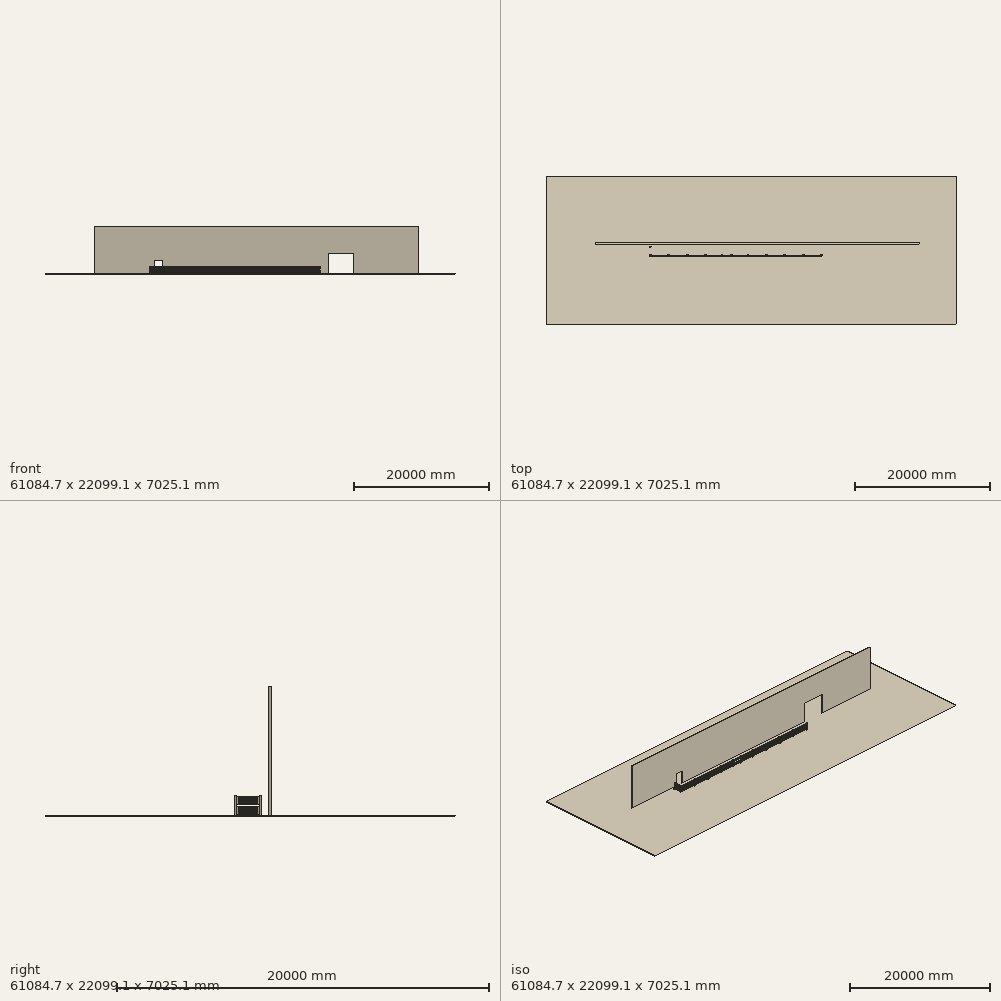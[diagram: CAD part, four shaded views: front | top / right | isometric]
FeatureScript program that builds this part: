
annotation { "Feature Type Name" : "Feature", "Feature Type Description" : "" }
export const myFeature = defineFeature(function(context is Context, id is Id, definition is map)
    precondition{}
    {
        {
            var Q0;
            Q0=qCreatedBy(makeId("Front.planeOp"),FACE);
            var sketch = newSketch(context, id + "F0", { "sketchPlane" : qUnion([Q0])});
            skLineSegment(sketch, "E0.bottom", {"start": v(-8708.65, 6974.33) * mm, "end": v(39551.35, 6974.33) * mm});
            skLineSegment(sketch, "E0.top", {"start": v(-8708.65, 0) * mm, "end": v(181.35, 0) * mm});
            skLineSegment(sketch, "E0.left", {"start": v(-8708.65, 6974.33) * mm, "end": v(-8708.65, 0) * mm});
            skLineSegment(sketch, "E0.right", {"start": v(39551.35, 6974.33) * mm, "end": v(39551.35, 0) * mm});
            skLineSegment(sketch, "E1.bottom", {"start": v(181.35, 1981.2) * mm, "end": v(1400.55, 1981.2) * mm});
            skLineSegment(sketch, "E1.left", {"start": v(181.35, 1981.2) * mm, "end": v(181.35, 0) * mm});
            skLineSegment(sketch, "E1.right", {"start": v(1400.55, 1981.2) * mm, "end": v(1400.55, 0) * mm});
            skLineSegment(sketch, "E2.trimOffspring", {"start": v(1400.55, 0) * mm, "end": v(26165.55, 0) * mm});
            skLineSegment(sketch, "E3.bottom", {"start": v(26165.55, 3048) * mm, "end": v(29823.15, 3048) * mm});
            skLineSegment(sketch, "E3.left", {"start": v(26165.55, 3048) * mm, "end": v(26165.55, 0) * mm});
            skLineSegment(sketch, "E3.right", {"start": v(29823.15, 3048) * mm, "end": v(29823.15, 0) * mm});
            skLineSegment(sketch, "E4.trimOffspring", {"start": v(29823.15, 0) * mm, "end": v(39551.35, 0) * mm});
            skSolve(sketch);
        }
        {
            var Q0;
            Q0 = qSketchRegion(id + "F0", true);
            extrude(context, id + "F1", {"entities" : qUnion([Q0]), "oppositeDirection" : true, "depth" : 152.4 * mm, "offsetDistance" : 25.4 * mm});
        }
        {
            var Q0;
            Q0=qCreatedBy(makeId("Top.planeOp"),FACE);
            var sketch = newSketch(context, id + "F2", { "sketchPlane" : qUnion([Q0])});
            skLineSegment(sketch, "E5.bottom", {"start": v(-16039.74, 10082.5) * mm, "end": v(45045, 10082.5) * mm});
            skLineSegment(sketch, "E5.top", {"start": v(-16039.74, -12016.58) * mm, "end": v(45045, -12016.58) * mm});
            skLineSegment(sketch, "E5.left", {"start": v(-16039.74, 10082.5) * mm, "end": v(-16039.74, -12016.58) * mm});
            skLineSegment(sketch, "E5.right", {"start": v(45045, 10082.5) * mm, "end": v(45045, -12016.58) * mm});
            skSolve(sketch);
        }
        {
            var Q0;
            Q0 = qSketchRegion(id + "F2", true);
            extrude(context, id + "F3", {"entities" : qUnion([Q0]), "oppositeDirection" : true, "depth" : 50.8 * mm, "offsetDistance" : 25.4 * mm});
        }
        {
            var Q0;
            Q0=makeQuery(id+"F3.opExtrude","CAP_FACE",FACE,{"disambiguationData":[OSD([sQuery(id+"F2.wireOp",EDGE,"E5.bottom"),sQuery(id+"F2.wireOp",EDGE,"E5.top"),sQuery(id+"F2.wireOp",EDGE,"E5.left"),sQuery(id+"F2.wireOp",EDGE,"E5.right")])],"isStart":true});
            var sketch = newSketch(context, id + "F4", { "sketchPlane" : qUnion([Q0])});
            skLineSegment(sketch, "E6.bottom", {"start": v(-682.25, -1625.6) * mm, "end": v(-428.25, -1625.6) * mm});
            skLineSegment(sketch, "E6.top", {"start": v(-682.25, -1879.6) * mm, "end": v(-428.25, -1879.6) * mm});
            skLineSegment(sketch, "E6.left", {"start": v(-682.25, -1625.6) * mm, "end": v(-682.25, -1879.6) * mm});
            skLineSegment(sketch, "E6.right", {"start": v(-428.25, -1625.6) * mm, "end": v(-428.25, -1879.6) * mm});
            skLineSegment(sketch, "E7.bottom", {"start": v(-682.25, -304.8) * mm, "end": v(-428.25, -304.8) * mm});
            skLineSegment(sketch, "E7.top", {"start": v(-682.25, -558.8) * mm, "end": v(-428.25, -558.8) * mm});
            skLineSegment(sketch, "E7.left", {"start": v(-682.25, -304.8) * mm, "end": v(-682.25, -558.8) * mm});
            skLineSegment(sketch, "E7.right", {"start": v(-428.25, -304.8) * mm, "end": v(-428.25, -558.8) * mm});
            skLineSegment(sketch, "E8.bottom", {"start": v(2060.95, -1625.6) * mm, "end": v(2314.95, -1625.6) * mm});
            skLineSegment(sketch, "E8.top", {"start": v(2060.95, -1879.6) * mm, "end": v(2314.95, -1879.6) * mm});
            skLineSegment(sketch, "E8.left", {"start": v(2060.95, -1625.6) * mm, "end": v(2060.95, -1879.6) * mm});
            skLineSegment(sketch, "E8.right", {"start": v(2314.95, -1625.6) * mm, "end": v(2314.95, -1879.6) * mm});
            skLineSegment(sketch, "E9.bottom", {"start": v(4804.15, -1625.6) * mm, "end": v(5058.15, -1625.6) * mm});
            skLineSegment(sketch, "E9.top", {"start": v(4804.15, -1879.6) * mm, "end": v(5058.15, -1879.6) * mm});
            skLineSegment(sketch, "E9.left", {"start": v(4804.15, -1625.6) * mm, "end": v(4804.15, -1879.6) * mm});
            skLineSegment(sketch, "E9.right", {"start": v(5058.15, -1625.6) * mm, "end": v(5058.15, -1879.6) * mm});
            skLineSegment(sketch, "E10.bottom", {"start": v(7547.35, -1625.6) * mm, "end": v(7801.35, -1625.6) * mm});
            skLineSegment(sketch, "E10.top", {"start": v(7547.35, -1879.6) * mm, "end": v(7801.35, -1879.6) * mm});
            skLineSegment(sketch, "E10.left", {"start": v(7547.35, -1625.6) * mm, "end": v(7547.35, -1879.6) * mm});
            skLineSegment(sketch, "E10.right", {"start": v(7801.35, -1625.6) * mm, "end": v(7801.35, -1879.6) * mm});
            skLineSegment(sketch, "E11.bottom", {"start": v(9985.75, -1625.6) * mm, "end": v(10239.75, -1625.6) * mm});
            skLineSegment(sketch, "E11.top", {"start": v(9985.75, -1879.6) * mm, "end": v(10239.75, -1879.6) * mm});
            skLineSegment(sketch, "E11.left", {"start": v(9985.75, -1625.6) * mm, "end": v(9985.75, -1879.6) * mm});
            skLineSegment(sketch, "E11.right", {"start": v(10239.75, -1625.6) * mm, "end": v(10239.75, -1879.6) * mm});
            skLineSegment(sketch, "E12.bottom", {"start": v(11408.15, -1625.6) * mm, "end": v(11662.15, -1625.6) * mm});
            skLineSegment(sketch, "E12.top", {"start": v(11408.15, -1879.6) * mm, "end": v(11662.15, -1879.6) * mm});
            skLineSegment(sketch, "E12.left", {"start": v(11408.15, -1625.6) * mm, "end": v(11408.15, -1879.6) * mm});
            skLineSegment(sketch, "E12.right", {"start": v(11662.15, -1625.6) * mm, "end": v(11662.15, -1879.6) * mm});
            skSolve(sketch);
        }
        {
            var Q0;
            Q0 = qSketchRegion(id + "F4", true);
            extrude(context, id + "F5", {"entities" : qUnion([Q0]), "depth" : 15.88 * mm, "offsetDistance" : 25.4 * mm});
        }
        {
            var Q0;
            Q0=makeQuery(id+"F5.opExtrude","CAP_FACE",FACE,{"disambiguationData":[OSD([sQuery(id+"F4.wireOp",EDGE,"E7.bottom"),sQuery(id+"F4.wireOp",EDGE,"E7.top"),sQuery(id+"F4.wireOp",EDGE,"E7.left"),sQuery(id+"F4.wireOp",EDGE,"E7.right")])],"isStart":false});
            var sketch = newSketch(context, id + "F6", { "sketchPlane" : qUnion([Q0])});
            skLineSegment(sketch, "E13.bottom", {"start": v(-606.05, -381) * mm, "end": v(-504.45, -381) * mm});
            skLineSegment(sketch, "E13.top", {"start": v(-606.05, -482.6) * mm, "end": v(-504.45, -482.6) * mm});
            skLineSegment(sketch, "E13.left", {"start": v(-606.05, -381) * mm, "end": v(-606.05, -482.6) * mm});
            skLineSegment(sketch, "E13.right", {"start": v(-504.45, -381) * mm, "end": v(-504.45, -482.6) * mm});
            skLineSegment(sketch, "E14.bottom", {"start": v(-606.05, -1701.8) * mm, "end": v(-504.45, -1701.8) * mm});
            skLineSegment(sketch, "E14.top", {"start": v(-606.05, -1803.4) * mm, "end": v(-504.45, -1803.4) * mm});
            skLineSegment(sketch, "E14.left", {"start": v(-606.05, -1701.8) * mm, "end": v(-606.05, -1803.4) * mm});
            skLineSegment(sketch, "E14.right", {"start": v(-504.45, -1701.8) * mm, "end": v(-504.45, -1803.4) * mm});
            skLineSegment(sketch, "E15.bottom", {"start": v(2137.15, -1701.8) * mm, "end": v(2238.75, -1701.8) * mm});
            skLineSegment(sketch, "E15.top", {"start": v(2137.15, -1803.4) * mm, "end": v(2238.75, -1803.4) * mm});
            skLineSegment(sketch, "E15.left", {"start": v(2137.15, -1701.8) * mm, "end": v(2137.15, -1803.4) * mm});
            skLineSegment(sketch, "E15.right", {"start": v(2238.75, -1701.8) * mm, "end": v(2238.75, -1803.4) * mm});
            skLineSegment(sketch, "E16.bottom", {"start": v(4880.35, -1701.8) * mm, "end": v(4981.95, -1701.8) * mm});
            skLineSegment(sketch, "E16.top", {"start": v(4880.35, -1803.4) * mm, "end": v(4981.95, -1803.4) * mm});
            skLineSegment(sketch, "E16.left", {"start": v(4880.35, -1701.8) * mm, "end": v(4880.35, -1803.4) * mm});
            skLineSegment(sketch, "E16.right", {"start": v(4981.95, -1701.8) * mm, "end": v(4981.95, -1803.4) * mm});
            skLineSegment(sketch, "E17.bottom", {"start": v(7623.55, -1701.8) * mm, "end": v(7725.15, -1701.8) * mm});
            skLineSegment(sketch, "E17.top", {"start": v(7623.55, -1803.4) * mm, "end": v(7725.15, -1803.4) * mm});
            skLineSegment(sketch, "E17.left", {"start": v(7623.55, -1701.8) * mm, "end": v(7623.55, -1803.4) * mm});
            skLineSegment(sketch, "E17.right", {"start": v(7725.15, -1701.8) * mm, "end": v(7725.15, -1803.4) * mm});
            skLineSegment(sketch, "E18.bottom", {"start": v(10061.95, -1701.8) * mm, "end": v(10163.55, -1701.8) * mm});
            skLineSegment(sketch, "E18.top", {"start": v(10061.95, -1803.4) * mm, "end": v(10163.55, -1803.4) * mm});
            skLineSegment(sketch, "E18.left", {"start": v(10061.95, -1701.8) * mm, "end": v(10061.95, -1803.4) * mm});
            skLineSegment(sketch, "E18.right", {"start": v(10163.55, -1701.8) * mm, "end": v(10163.55, -1803.4) * mm});
            skLineSegment(sketch, "E19.bottom", {"start": v(11484.35, -1701.8) * mm, "end": v(11585.95, -1701.8) * mm});
            skLineSegment(sketch, "E19.top", {"start": v(11484.35, -1803.4) * mm, "end": v(11585.95, -1803.4) * mm});
            skLineSegment(sketch, "E19.left", {"start": v(11484.35, -1701.8) * mm, "end": v(11484.35, -1803.4) * mm});
            skLineSegment(sketch, "E19.right", {"start": v(11585.95, -1701.8) * mm, "end": v(11585.95, -1803.4) * mm});
            skSolve(sketch);
        }
        {
            var Q0;
            Q0 = qSketchRegion(id + "F6", true);
            extrude(context, id + "F7", {"entities" : qUnion([Q0]), "operationType" : NewBodyOperationType.ADD, "depth" : 1066.8 * mm, "offsetDistance" : 25.4 * mm});
        }
        {
            var Q0;
            Q0=makeQuery(id+"F7.opExtrude","CAP_FACE",FACE,{"disambiguationData":[OSD([sQuery(id+"F6.wireOp",EDGE,"E13.bottom"),sQuery(id+"F6.wireOp",EDGE,"E13.top"),sQuery(id+"F6.wireOp",EDGE,"E13.left"),sQuery(id+"F6.wireOp",EDGE,"E13.right")])],"isStart":false});
            cPlane(context, id + "F8", {"entities" : qUnion([Q0]), "cplaneType" : CPlaneType.OFFSET, "offset" : 15.88 * mm, "width" : 152.4 * mm, "height" : 152.4 * mm});
        }
        {
            var Q0;
            Q0=qCreatedBy(id+"F8.planeOp",FACE);
            var sketch = newSketch(context, id + "F9", { "sketchPlane" : qUnion([Q0])});
            skLineSegment(sketch, "E20.bottom", {"start": v(-599.7, -387.35) * mm, "end": v(-510.8, -387.35) * mm});
            skLineSegment(sketch, "E20.top", {"start": v(-599.7, -476.25) * mm, "end": v(-510.8, -476.25) * mm});
            skLineSegment(sketch, "E20.left", {"start": v(-599.7, -387.35) * mm, "end": v(-599.7, -476.25) * mm});
            skLineSegment(sketch, "E20.right", {"start": v(-510.8, -387.35) * mm, "end": v(-510.8, -476.25) * mm});
            skLineSegment(sketch, "E21.bottom", {"start": v(-599.7, -1708.15) * mm, "end": v(-510.8, -1708.15) * mm});
            skLineSegment(sketch, "E21.top", {"start": v(-599.7, -1797.05) * mm, "end": v(-510.8, -1797.05) * mm});
            skLineSegment(sketch, "E21.left", {"start": v(-599.7, -1708.15) * mm, "end": v(-599.7, -1797.05) * mm});
            skLineSegment(sketch, "E21.right", {"start": v(-510.8, -1708.15) * mm, "end": v(-510.8, -1797.05) * mm});
            skLineSegment(sketch, "E22.bottom", {"start": v(2143.5, -1708.15) * mm, "end": v(2232.4, -1708.15) * mm});
            skLineSegment(sketch, "E22.top", {"start": v(2143.5, -1797.05) * mm, "end": v(2232.4, -1797.05) * mm});
            skLineSegment(sketch, "E22.left", {"start": v(2143.5, -1708.15) * mm, "end": v(2143.5, -1797.05) * mm});
            skLineSegment(sketch, "E22.right", {"start": v(2232.4, -1708.15) * mm, "end": v(2232.4, -1797.05) * mm});
            skLineSegment(sketch, "E23.bottom", {"start": v(4886.7, -1708.15) * mm, "end": v(4975.6, -1708.15) * mm});
            skLineSegment(sketch, "E23.top", {"start": v(4886.7, -1797.05) * mm, "end": v(4975.6, -1797.05) * mm});
            skLineSegment(sketch, "E23.left", {"start": v(4886.7, -1708.15) * mm, "end": v(4886.7, -1797.05) * mm});
            skLineSegment(sketch, "E23.right", {"start": v(4975.6, -1708.15) * mm, "end": v(4975.6, -1797.05) * mm});
            skLineSegment(sketch, "E24.bottom", {"start": v(7629.9, -1708.15) * mm, "end": v(7718.8, -1708.15) * mm});
            skLineSegment(sketch, "E24.top", {"start": v(7629.9, -1797.05) * mm, "end": v(7718.8, -1797.05) * mm});
            skLineSegment(sketch, "E24.left", {"start": v(7629.9, -1708.15) * mm, "end": v(7629.9, -1797.05) * mm});
            skLineSegment(sketch, "E24.right", {"start": v(7718.8, -1708.15) * mm, "end": v(7718.8, -1797.05) * mm});
            skLineSegment(sketch, "E25.bottom", {"start": v(10068.3, -1708.15) * mm, "end": v(10157.2, -1708.15) * mm});
            skLineSegment(sketch, "E25.top", {"start": v(10068.3, -1797.05) * mm, "end": v(10157.2, -1797.05) * mm});
            skLineSegment(sketch, "E25.left", {"start": v(10068.3, -1708.15) * mm, "end": v(10068.3, -1797.05) * mm});
            skLineSegment(sketch, "E25.right", {"start": v(10157.2, -1708.15) * mm, "end": v(10157.2, -1797.05) * mm});
            skLineSegment(sketch, "E26.bottom", {"start": v(11490.7, -1708.15) * mm, "end": v(11579.6, -1708.15) * mm});
            skLineSegment(sketch, "E26.top", {"start": v(11490.7, -1797.05) * mm, "end": v(11579.6, -1797.05) * mm});
            skLineSegment(sketch, "E26.left", {"start": v(11490.7, -1708.15) * mm, "end": v(11490.7, -1797.05) * mm});
            skLineSegment(sketch, "E26.right", {"start": v(11579.6, -1708.15) * mm, "end": v(11579.6, -1797.05) * mm});
            skSolve(sketch);
        }
        {
            var Q0;
            Q0 = qSketchRegion(id + "F9", true);
            extrude(context, id + "F10", {"entities" : qUnion([Q0]), "endBound" : BoundingType.UP_TO_NEXT, "oppositeDirection" : true, "depth" : 25.4 * mm, "offsetDistance" : 25.4 * mm, "hasDraft" : true, "draftAngle" : 21.8 * degree});
        }
        {
            var Q0;
            Q0=makeQuery(id+"F10.opExtrude","CAP_FACE",FACE,{"disambiguationData":[OSD([sQuery(id+"F9.wireOp",EDGE,"E20.bottom"),sQuery(id+"F9.wireOp",EDGE,"E20.top"),sQuery(id+"F9.wireOp",EDGE,"E20.left"),sQuery(id+"F9.wireOp",EDGE,"E20.right")])],"isStart":true});
            cPlane(context, id + "F11", {"entities" : qUnion([Q0]), "cplaneType" : CPlaneType.OFFSET, "offset" : 50.8 * mm, "oppositeDirection" : true, "width" : 152.4 * mm, "height" : 152.4 * mm});
        }
        {
            var Q0;
            Q0=qCreatedBy(id+"F11.planeOp",FACE);
            var sketch = newSketch(context, id + "F12", { "sketchPlane" : qUnion([Q0])});
            skLineSegment(sketch, "E27.bottom", {"start": v(-602.87, -482.6) * mm, "end": v(-507.62, -482.6) * mm});
            skLineSegment(sketch, "E27.top", {"start": v(-602.87, -577.85) * mm, "end": v(-507.62, -577.85) * mm});
            skLineSegment(sketch, "E27.left", {"start": v(-602.87, -482.6) * mm, "end": v(-602.87, -577.85) * mm});
            skLineSegment(sketch, "E27.right", {"start": v(-507.62, -482.6) * mm, "end": v(-507.62, -577.85) * mm});
            skLineSegment(sketch, "E28.bottom", {"start": v(-602.87, -1606.55) * mm, "end": v(-507.62, -1606.55) * mm});
            skLineSegment(sketch, "E28.top", {"start": v(-602.87, -1701.8) * mm, "end": v(-507.62, -1701.8) * mm});
            skLineSegment(sketch, "E28.left", {"start": v(-602.87, -1606.55) * mm, "end": v(-602.87, -1701.8) * mm});
            skLineSegment(sketch, "E28.right", {"start": v(-507.62, -1606.55) * mm, "end": v(-507.62, -1701.8) * mm});
            skLineSegment(sketch, "E29.bottom", {"start": v(-504.45, -1704.97) * mm, "end": v(-409.2, -1704.97) * mm});
            skLineSegment(sketch, "E29.top", {"start": v(-504.45, -1800.22) * mm, "end": v(-409.2, -1800.22) * mm});
            skLineSegment(sketch, "E29.left", {"start": v(-504.45, -1704.97) * mm, "end": v(-504.45, -1800.22) * mm});
            skLineSegment(sketch, "E29.right", {"start": v(-409.2, -1704.97) * mm, "end": v(-409.2, -1800.22) * mm});
            skLineSegment(sketch, "E30.bottom", {"start": v(2041.9, -1704.97) * mm, "end": v(2137.15, -1704.97) * mm});
            skLineSegment(sketch, "E30.top", {"start": v(2041.9, -1800.22) * mm, "end": v(2137.15, -1800.22) * mm});
            skLineSegment(sketch, "E30.left", {"start": v(2041.9, -1704.97) * mm, "end": v(2041.9, -1800.22) * mm});
            skLineSegment(sketch, "E30.right", {"start": v(2137.15, -1704.97) * mm, "end": v(2137.15, -1800.22) * mm});
            skLineSegment(sketch, "E31.bottom", {"start": v(2238.75, -1704.97) * mm, "end": v(2334, -1704.97) * mm});
            skLineSegment(sketch, "E31.top", {"start": v(2238.75, -1800.22) * mm, "end": v(2334, -1800.22) * mm});
            skLineSegment(sketch, "E31.left", {"start": v(2238.75, -1704.97) * mm, "end": v(2238.75, -1800.22) * mm});
            skLineSegment(sketch, "E31.right", {"start": v(2334, -1704.97) * mm, "end": v(2334, -1800.22) * mm});
            skLineSegment(sketch, "E32.bottom", {"start": v(4785.1, -1704.97) * mm, "end": v(4880.35, -1704.97) * mm});
            skLineSegment(sketch, "E32.top", {"start": v(4785.1, -1800.22) * mm, "end": v(4880.35, -1800.22) * mm});
            skLineSegment(sketch, "E32.left", {"start": v(4785.1, -1704.97) * mm, "end": v(4785.1, -1800.22) * mm});
            skLineSegment(sketch, "E32.right", {"start": v(4880.35, -1704.97) * mm, "end": v(4880.35, -1800.22) * mm});
            skLineSegment(sketch, "E33.bottom", {"start": v(4981.95, -1704.97) * mm, "end": v(5077.2, -1704.97) * mm});
            skLineSegment(sketch, "E33.top", {"start": v(4981.95, -1800.22) * mm, "end": v(5077.2, -1800.22) * mm});
            skLineSegment(sketch, "E33.left", {"start": v(4981.95, -1704.97) * mm, "end": v(4981.95, -1800.22) * mm});
            skLineSegment(sketch, "E33.right", {"start": v(5077.2, -1704.97) * mm, "end": v(5077.2, -1800.22) * mm});
            skLineSegment(sketch, "E34.bottom", {"start": v(7528.3, -1704.98) * mm, "end": v(7623.55, -1704.98) * mm});
            skLineSegment(sketch, "E34.top", {"start": v(7528.3, -1800.23) * mm, "end": v(7623.55, -1800.23) * mm});
            skLineSegment(sketch, "E34.left", {"start": v(7528.3, -1704.98) * mm, "end": v(7528.3, -1800.23) * mm});
            skLineSegment(sketch, "E34.right", {"start": v(7623.55, -1704.98) * mm, "end": v(7623.55, -1800.23) * mm});
            skLineSegment(sketch, "E35.bottom", {"start": v(7725.15, -1704.98) * mm, "end": v(7820.4, -1704.98) * mm});
            skLineSegment(sketch, "E35.top", {"start": v(7725.15, -1800.23) * mm, "end": v(7820.4, -1800.23) * mm});
            skLineSegment(sketch, "E35.left", {"start": v(7725.15, -1704.98) * mm, "end": v(7725.15, -1800.23) * mm});
            skLineSegment(sketch, "E35.right", {"start": v(7820.4, -1704.98) * mm, "end": v(7820.4, -1800.23) * mm});
            skLineSegment(sketch, "E36.bottom", {"start": v(9966.7, -1704.97) * mm, "end": v(10061.95, -1704.97) * mm});
            skLineSegment(sketch, "E36.top", {"start": v(9966.7, -1800.22) * mm, "end": v(10061.95, -1800.22) * mm});
            skLineSegment(sketch, "E36.left", {"start": v(9966.7, -1704.97) * mm, "end": v(9966.7, -1800.22) * mm});
            skLineSegment(sketch, "E36.right", {"start": v(10061.95, -1704.97) * mm, "end": v(10061.95, -1800.22) * mm});
            skSolve(sketch);
        }
        {
            var Q0;
            Q0 = qSketchRegion(id + "F12", true);
            extrude(context, id + "F13", {"entities" : qUnion([Q0]), "oppositeDirection" : true, "depth" : 457.2 * mm, "offsetDistance" : 25.4 * mm});
        }
        {
            var Q0;
            Q0=makeQuery(id+"F13.opExtrude","CAP_FACE",FACE,{"disambiguationData":[OSD([sQuery(id+"F12.wireOp",EDGE,"E27.bottom"),sQuery(id+"F12.wireOp",EDGE,"E27.top"),sQuery(id+"F12.wireOp",EDGE,"E27.left"),sQuery(id+"F12.wireOp",EDGE,"E27.right")])],"isStart":true});
            var Q1;
            Q1=makeQuery(id+"F13.opExtrude","SWEPT_FACE",FACE,{"disambiguationData":[OSD([sQuery(id+"F12.wireOp",EDGE,"E27.top")])]});
            var Q2;
            Q2=makeQuery(id+"F13.opExtrude","CAP_FACE",FACE,{"disambiguationData":[OSD([sQuery(id+"F12.wireOp",EDGE,"E28.bottom"),sQuery(id+"F12.wireOp",EDGE,"E28.top"),sQuery(id+"F12.wireOp",EDGE,"E28.left"),sQuery(id+"F12.wireOp",EDGE,"E28.right")])],"isStart":true});
            var Q3;
            Q3=makeQuery(id+"F13.opExtrude","SWEPT_FACE",FACE,{"disambiguationData":[OSD([sQuery(id+"F12.wireOp",EDGE,"E28.bottom")])]});
            var Q4;
            Q4=makeQuery(id+"F13.opExtrude","CAP_FACE",FACE,{"disambiguationData":[OSD([sQuery(id+"F12.wireOp",EDGE,"E29.bottom"),sQuery(id+"F12.wireOp",EDGE,"E29.top"),sQuery(id+"F12.wireOp",EDGE,"E29.left"),sQuery(id+"F12.wireOp",EDGE,"E29.right")])],"isStart":true});
            var Q5;
            Q5=makeQuery(id+"F13.opExtrude","SWEPT_FACE",FACE,{"disambiguationData":[OSD([sQuery(id+"F12.wireOp",EDGE,"E29.right")])]});
            var Q6;
            Q6=makeQuery(id+"F13.opExtrude","CAP_FACE",FACE,{"disambiguationData":[OSD([sQuery(id+"F12.wireOp",EDGE,"E30.bottom"),sQuery(id+"F12.wireOp",EDGE,"E30.top"),sQuery(id+"F12.wireOp",EDGE,"E30.left"),sQuery(id+"F12.wireOp",EDGE,"E30.right")])],"isStart":true});
            var Q7;
            Q7=makeQuery(id+"F13.opExtrude","SWEPT_FACE",FACE,{"disambiguationData":[OSD([sQuery(id+"F12.wireOp",EDGE,"E30.left")])]});
            var Q8;
            Q8=makeQuery(id+"F13.opExtrude","CAP_FACE",FACE,{"disambiguationData":[OSD([sQuery(id+"F12.wireOp",EDGE,"E31.bottom"),sQuery(id+"F12.wireOp",EDGE,"E31.top"),sQuery(id+"F12.wireOp",EDGE,"E31.left"),sQuery(id+"F12.wireOp",EDGE,"E31.right")])],"isStart":true});
            var Q9;
            Q9=makeQuery(id+"F13.opExtrude","SWEPT_FACE",FACE,{"disambiguationData":[OSD([sQuery(id+"F12.wireOp",EDGE,"E31.right")])]});
            var Q10;
            Q10=makeQuery(id+"F13.opExtrude","SWEPT_FACE",FACE,{"disambiguationData":[OSD([sQuery(id+"F12.wireOp",EDGE,"E32.left")])]});
            var Q11;
            Q11=makeQuery(id+"F13.opExtrude","CAP_FACE",FACE,{"disambiguationData":[OSD([sQuery(id+"F12.wireOp",EDGE,"E32.bottom"),sQuery(id+"F12.wireOp",EDGE,"E32.top"),sQuery(id+"F12.wireOp",EDGE,"E32.left"),sQuery(id+"F12.wireOp",EDGE,"E32.right")])],"isStart":true});
            var Q12;
            Q12=makeQuery(id+"F13.opExtrude","CAP_FACE",FACE,{"disambiguationData":[OSD([sQuery(id+"F12.wireOp",EDGE,"E33.bottom"),sQuery(id+"F12.wireOp",EDGE,"E33.top"),sQuery(id+"F12.wireOp",EDGE,"E33.left"),sQuery(id+"F12.wireOp",EDGE,"E33.right")])],"isStart":true});
            var Q13;
            Q13=makeQuery(id+"F13.opExtrude","SWEPT_FACE",FACE,{"disambiguationData":[OSD([sQuery(id+"F12.wireOp",EDGE,"E33.right")])]});
            var Q14;
            Q14=makeQuery(id+"F13.opExtrude","SWEPT_FACE",FACE,{"disambiguationData":[OSD([sQuery(id+"F12.wireOp",EDGE,"E35.right")])]});
            var Q15;
            Q15=makeQuery(id+"F13.opExtrude","CAP_FACE",FACE,{"disambiguationData":[OSD([sQuery(id+"F12.wireOp",EDGE,"E35.bottom"),sQuery(id+"F12.wireOp",EDGE,"E35.top"),sQuery(id+"F12.wireOp",EDGE,"E35.left"),sQuery(id+"F12.wireOp",EDGE,"E35.right")])],"isStart":true});
            var Q16;
            Q16=makeQuery(id+"F13.opExtrude","CAP_FACE",FACE,{"disambiguationData":[OSD([sQuery(id+"F12.wireOp",EDGE,"E34.bottom"),sQuery(id+"F12.wireOp",EDGE,"E34.top"),sQuery(id+"F12.wireOp",EDGE,"E34.left"),sQuery(id+"F12.wireOp",EDGE,"E34.right")])],"isStart":true});
            var Q17;
            Q17=makeQuery(id+"F13.opExtrude","SWEPT_FACE",FACE,{"disambiguationData":[OSD([sQuery(id+"F12.wireOp",EDGE,"E34.left")])]});
            var Q18;
            Q18=makeQuery(id+"F13.opExtrude","CAP_FACE",FACE,{"disambiguationData":[OSD([sQuery(id+"F12.wireOp",EDGE,"f9b453c7-bccf-4bfe-9174-c25113f24e84.bottom"),sQuery(id+"F12.wireOp",EDGE,"f9b453c7-bccf-4bfe-9174-c25113f24e84.top"),sQuery(id+"F12.wireOp",EDGE,"f9b453c7-bccf-4bfe-9174-c25113f24e84.left"),sQuery(id+"F12.wireOp",EDGE,"f9b453c7-bccf-4bfe-9174-c25113f24e84.right")])],"isStart":true});
            var Q19;
            Q19=makeQuery(id+"F13.opExtrude","SWEPT_FACE",FACE,{"disambiguationData":[OSD([sQuery(id+"F12.wireOp",EDGE,"449fd35b-e63b-4b74-898c-2944b7ca5cd8.right")])]});
            var Q20;
            Q20=makeQuery(id+"F13.opExtrude","CAP_FACE",FACE,{"disambiguationData":[OSD([sQuery(id+"F12.wireOp",EDGE,"449fd35b-e63b-4b74-898c-2944b7ca5cd8.bottom"),sQuery(id+"F12.wireOp",EDGE,"449fd35b-e63b-4b74-898c-2944b7ca5cd8.top"),sQuery(id+"F12.wireOp",EDGE,"449fd35b-e63b-4b74-898c-2944b7ca5cd8.left"),sQuery(id+"F12.wireOp",EDGE,"449fd35b-e63b-4b74-898c-2944b7ca5cd8.right")])],"isStart":true});
            var Q21;
            Q21=makeQuery(id+"F13.opExtrude","CAP_FACE",FACE,{"disambiguationData":[OSD([sQuery(id+"F12.wireOp",EDGE,"E36.bottom"),sQuery(id+"F12.wireOp",EDGE,"E36.top"),sQuery(id+"F12.wireOp",EDGE,"E36.left"),sQuery(id+"F12.wireOp",EDGE,"E36.right")])],"isStart":true});
            var Q22;
            Q22=makeQuery(id+"F13.opExtrude","SWEPT_FACE",FACE,{"disambiguationData":[OSD([sQuery(id+"F12.wireOp",EDGE,"E36.left")])]});
            var Q23;
            Q23=makeQuery(id+"F13.opExtrude","SWEPT_FACE",FACE,{"disambiguationData":[OSD([sQuery(id+"F12.wireOp",EDGE,"f9b453c7-bccf-4bfe-9174-c25113f24e84.left")])]});
            shell(context, id + "F14", {"entities" : qUnion([Q0, Q1, Q2, Q3, Q4, Q5, Q6, Q7, Q8, Q9, Q10, Q11, Q12, Q13, Q14, Q15, Q16, Q17, Q18, Q19, Q20, Q21, Q22, Q23]), "thickness" : 3.17 * mm});
        }
        {
            var Q0;
            Q0=qCreatedBy(id+"F11.planeOp",FACE);
            cPlane(context, id + "F15", {"entities" : qUnion([Q0]), "cplaneType" : CPlaneType.OFFSET, "offset" : 532.26 * mm, "oppositeDirection" : true, "width" : 152.4 * mm, "height" : 152.4 * mm});
        }
        {
            var Q0;
            Q0=qCreatedBy(id+"F15.planeOp",FACE);
            var sketch = newSketch(context, id + "F16", { "sketchPlane" : qUnion([Q0])});
            skLineSegment(sketch, "E37.bottom", {"start": v(-602.87, -482.6) * mm, "end": v(-507.62, -482.6) * mm});
            skLineSegment(sketch, "E37.top", {"start": v(-602.87, -577.85) * mm, "end": v(-507.62, -577.85) * mm});
            skLineSegment(sketch, "E37.left", {"start": v(-602.87, -482.6) * mm, "end": v(-602.87, -577.85) * mm});
            skLineSegment(sketch, "E37.right", {"start": v(-507.62, -482.6) * mm, "end": v(-507.62, -577.85) * mm});
            skLineSegment(sketch, "E38.bottom", {"start": v(-602.87, -1606.55) * mm, "end": v(-507.62, -1606.55) * mm});
            skLineSegment(sketch, "E38.top", {"start": v(-602.87, -1701.8) * mm, "end": v(-507.62, -1701.8) * mm});
            skLineSegment(sketch, "E38.left", {"start": v(-602.87, -1606.55) * mm, "end": v(-602.87, -1701.8) * mm});
            skLineSegment(sketch, "E38.right", {"start": v(-507.62, -1606.55) * mm, "end": v(-507.62, -1701.8) * mm});
            skLineSegment(sketch, "E39.bottom", {"start": v(-504.45, -1704.98) * mm, "end": v(-409.2, -1704.98) * mm});
            skLineSegment(sketch, "E39.top", {"start": v(-504.45, -1800.23) * mm, "end": v(-409.2, -1800.23) * mm});
            skLineSegment(sketch, "E39.left", {"start": v(-504.45, -1704.98) * mm, "end": v(-504.45, -1800.23) * mm});
            skLineSegment(sketch, "E39.right", {"start": v(-409.2, -1704.98) * mm, "end": v(-409.2, -1800.23) * mm});
            skLineSegment(sketch, "E40.bottom", {"start": v(2041.9, -1704.98) * mm, "end": v(2137.15, -1704.98) * mm});
            skLineSegment(sketch, "E40.top", {"start": v(2041.9, -1800.23) * mm, "end": v(2137.15, -1800.23) * mm});
            skLineSegment(sketch, "E40.left", {"start": v(2041.9, -1704.98) * mm, "end": v(2041.9, -1800.23) * mm});
            skLineSegment(sketch, "E40.right", {"start": v(2137.15, -1704.98) * mm, "end": v(2137.15, -1800.23) * mm});
            skLineSegment(sketch, "E41.bottom", {"start": v(2238.75, -1704.98) * mm, "end": v(2334, -1704.98) * mm});
            skLineSegment(sketch, "E41.top", {"start": v(2238.75, -1800.23) * mm, "end": v(2334, -1800.23) * mm});
            skLineSegment(sketch, "E41.left", {"start": v(2238.75, -1704.98) * mm, "end": v(2238.75, -1800.23) * mm});
            skLineSegment(sketch, "E41.right", {"start": v(2334, -1704.98) * mm, "end": v(2334, -1800.23) * mm});
            skLineSegment(sketch, "E42.bottom", {"start": v(4785.1, -1704.98) * mm, "end": v(4880.35, -1704.98) * mm});
            skLineSegment(sketch, "E42.top", {"start": v(4785.1, -1800.23) * mm, "end": v(4880.35, -1800.23) * mm});
            skLineSegment(sketch, "E42.left", {"start": v(4785.1, -1704.98) * mm, "end": v(4785.1, -1800.23) * mm});
            skLineSegment(sketch, "E42.right", {"start": v(4880.35, -1704.98) * mm, "end": v(4880.35, -1800.23) * mm});
            skLineSegment(sketch, "E43.bottom", {"start": v(4981.95, -1704.97) * mm, "end": v(5077.2, -1704.97) * mm});
            skLineSegment(sketch, "E43.top", {"start": v(4981.95, -1800.23) * mm, "end": v(5077.2, -1800.23) * mm});
            skLineSegment(sketch, "E43.left", {"start": v(4981.95, -1704.98) * mm, "end": v(4981.95, -1800.23) * mm});
            skLineSegment(sketch, "E43.right", {"start": v(5077.2, -1704.97) * mm, "end": v(5077.2, -1800.23) * mm});
            skLineSegment(sketch, "E44.bottom", {"start": v(7528.3, -1704.98) * mm, "end": v(7623.55, -1704.98) * mm});
            skLineSegment(sketch, "E44.top", {"start": v(7528.3, -1800.23) * mm, "end": v(7623.55, -1800.23) * mm});
            skLineSegment(sketch, "E44.left", {"start": v(7528.3, -1704.98) * mm, "end": v(7528.3, -1800.23) * mm});
            skLineSegment(sketch, "E44.right", {"start": v(7623.55, -1704.98) * mm, "end": v(7623.55, -1800.23) * mm});
            skLineSegment(sketch, "E45.bottom", {"start": v(7725.15, -1704.97) * mm, "end": v(7820.4, -1704.97) * mm});
            skLineSegment(sketch, "E45.top", {"start": v(7725.15, -1800.23) * mm, "end": v(7820.4, -1800.23) * mm});
            skLineSegment(sketch, "E45.left", {"start": v(7725.15, -1704.98) * mm, "end": v(7725.15, -1800.23) * mm});
            skLineSegment(sketch, "E45.right", {"start": v(7820.4, -1704.98) * mm, "end": v(7820.4, -1800.23) * mm});
            skLineSegment(sketch, "E46.bottom", {"start": v(9966.7, -1704.97) * mm, "end": v(10061.95, -1704.97) * mm});
            skLineSegment(sketch, "E46.top", {"start": v(9966.7, -1800.22) * mm, "end": v(10061.95, -1800.22) * mm});
            skLineSegment(sketch, "E46.left", {"start": v(9966.7, -1704.97) * mm, "end": v(9966.7, -1800.22) * mm});
            skLineSegment(sketch, "E46.right", {"start": v(10061.95, -1704.97) * mm, "end": v(10061.95, -1800.22) * mm});
            skSolve(sketch);
        }
        {
            var Q0;
            Q0 = qSketchRegion(id + "F16", true);
            extrude(context, id + "F17", {"entities" : qUnion([Q0]), "oppositeDirection" : true, "depth" : 457.2 * mm, "offsetDistance" : 25.4 * mm});
        }
        {
            var Q0;
            Q0=makeQuery(id+"F17.opExtrude","SWEPT_FACE",FACE,{"disambiguationData":[OSD([sQuery(id+"F16.wireOp",EDGE,"E37.top")])]});
            var Q1;
            Q1=makeQuery(id+"F17.opExtrude","CAP_FACE",FACE,{"disambiguationData":[OSD([sQuery(id+"F16.wireOp",EDGE,"E37.bottom"),sQuery(id+"F16.wireOp",EDGE,"E37.top"),sQuery(id+"F16.wireOp",EDGE,"E37.left"),sQuery(id+"F16.wireOp",EDGE,"E37.right")])],"isStart":true});
            var Q2;
            Q2=makeQuery(id+"F17.opExtrude","CAP_FACE",FACE,{"disambiguationData":[OSD([sQuery(id+"F16.wireOp",EDGE,"E38.bottom"),sQuery(id+"F16.wireOp",EDGE,"E38.top"),sQuery(id+"F16.wireOp",EDGE,"E38.left"),sQuery(id+"F16.wireOp",EDGE,"E38.right")])],"isStart":true});
            var Q3;
            Q3=makeQuery(id+"F17.opExtrude","SWEPT_FACE",FACE,{"disambiguationData":[OSD([sQuery(id+"F16.wireOp",EDGE,"E38.bottom")])]});
            var Q4;
            Q4=makeQuery(id+"F17.opExtrude","SWEPT_FACE",FACE,{"disambiguationData":[OSD([sQuery(id+"F16.wireOp",EDGE,"E40.left")])]});
            var Q5;
            Q5=makeQuery(id+"F17.opExtrude","CAP_FACE",FACE,{"disambiguationData":[OSD([sQuery(id+"F16.wireOp",EDGE,"E40.bottom"),sQuery(id+"F16.wireOp",EDGE,"E40.top"),sQuery(id+"F16.wireOp",EDGE,"E40.left"),sQuery(id+"F16.wireOp",EDGE,"E40.right")])],"isStart":true});
            var Q6;
            Q6=makeQuery(id+"F17.opExtrude","CAP_FACE",FACE,{"disambiguationData":[OSD([sQuery(id+"F16.wireOp",EDGE,"E41.bottom"),sQuery(id+"F16.wireOp",EDGE,"E41.top"),sQuery(id+"F16.wireOp",EDGE,"E41.left"),sQuery(id+"F16.wireOp",EDGE,"E41.right")])],"isStart":true});
            var Q7;
            Q7=makeQuery(id+"F17.opExtrude","SWEPT_FACE",FACE,{"disambiguationData":[OSD([sQuery(id+"F16.wireOp",EDGE,"E39.right")])]});
            var Q8;
            Q8=makeQuery(id+"F17.opExtrude","CAP_FACE",FACE,{"disambiguationData":[OSD([sQuery(id+"F16.wireOp",EDGE,"E39.bottom"),sQuery(id+"F16.wireOp",EDGE,"E39.top"),sQuery(id+"F16.wireOp",EDGE,"E39.left"),sQuery(id+"F16.wireOp",EDGE,"E39.right")])],"isStart":true});
            var Q9;
            Q9=makeQuery(id+"F17.opExtrude","SWEPT_FACE",FACE,{"disambiguationData":[OSD([sQuery(id+"F16.wireOp",EDGE,"E41.right")])]});
            var Q10;
            Q10=makeQuery(id+"F17.opExtrude","CAP_FACE",FACE,{"disambiguationData":[OSD([sQuery(id+"F16.wireOp",EDGE,"E42.bottom"),sQuery(id+"F16.wireOp",EDGE,"E42.top"),sQuery(id+"F16.wireOp",EDGE,"E42.left"),sQuery(id+"F16.wireOp",EDGE,"E42.right")])],"isStart":true});
            var Q11;
            Q11=makeQuery(id+"F17.opExtrude","SWEPT_FACE",FACE,{"disambiguationData":[OSD([sQuery(id+"F16.wireOp",EDGE,"E43.right")])]});
            var Q12;
            Q12=makeQuery(id+"F17.opExtrude","CAP_FACE",FACE,{"disambiguationData":[OSD([sQuery(id+"F16.wireOp",EDGE,"E43.bottom"),sQuery(id+"F16.wireOp",EDGE,"E43.top"),sQuery(id+"F16.wireOp",EDGE,"E43.left"),sQuery(id+"F16.wireOp",EDGE,"E43.right")])],"isStart":true});
            var Q13;
            Q13=makeQuery(id+"F17.opExtrude","CAP_FACE",FACE,{"disambiguationData":[OSD([sQuery(id+"F16.wireOp",EDGE,"E45.bottom"),sQuery(id+"F16.wireOp",EDGE,"E45.top"),sQuery(id+"F16.wireOp",EDGE,"E45.left"),sQuery(id+"F16.wireOp",EDGE,"E45.right")])],"isStart":true});
            var Q14;
            Q14=makeQuery(id+"F17.opExtrude","SWEPT_FACE",FACE,{"disambiguationData":[OSD([sQuery(id+"F16.wireOp",EDGE,"E45.right")])]});
            var Q15;
            Q15=makeQuery(id+"F17.opExtrude","CAP_FACE",FACE,{"disambiguationData":[OSD([sQuery(id+"F16.wireOp",EDGE,"E44.bottom"),sQuery(id+"F16.wireOp",EDGE,"E44.top"),sQuery(id+"F16.wireOp",EDGE,"E44.left"),sQuery(id+"F16.wireOp",EDGE,"E44.right")])],"isStart":true});
            var Q16;
            Q16=makeQuery(id+"F17.opExtrude","SWEPT_FACE",FACE,{"disambiguationData":[OSD([sQuery(id+"F16.wireOp",EDGE,"a3077837-2911-4114-b961-bef339efcebf.right")])]});
            var Q17;
            Q17=makeQuery(id+"F17.opExtrude","CAP_FACE",FACE,{"disambiguationData":[OSD([sQuery(id+"F16.wireOp",EDGE,"a3077837-2911-4114-b961-bef339efcebf.bottom"),sQuery(id+"F16.wireOp",EDGE,"a3077837-2911-4114-b961-bef339efcebf.top"),sQuery(id+"F16.wireOp",EDGE,"a3077837-2911-4114-b961-bef339efcebf.left"),sQuery(id+"F16.wireOp",EDGE,"a3077837-2911-4114-b961-bef339efcebf.right")])],"isStart":true});
            var Q18;
            Q18=makeQuery(id+"F17.opExtrude","CAP_FACE",FACE,{"disambiguationData":[OSD([sQuery(id+"F16.wireOp",EDGE,"E46.bottom"),sQuery(id+"F16.wireOp",EDGE,"E46.top"),sQuery(id+"F16.wireOp",EDGE,"E46.left"),sQuery(id+"F16.wireOp",EDGE,"E46.right")])],"isStart":true});
            var Q19;
            Q19=makeQuery(id+"F17.opExtrude","CAP_FACE",FACE,{"disambiguationData":[OSD([sQuery(id+"F16.wireOp",EDGE,"f3187e04-98a9-4826-9ade-0eccad066c5c.bottom"),sQuery(id+"F16.wireOp",EDGE,"f3187e04-98a9-4826-9ade-0eccad066c5c.top"),sQuery(id+"F16.wireOp",EDGE,"f3187e04-98a9-4826-9ade-0eccad066c5c.left"),sQuery(id+"F16.wireOp",EDGE,"f3187e04-98a9-4826-9ade-0eccad066c5c.right")])],"isStart":true});
            var Q20;
            Q20=makeQuery(id+"F17.opExtrude","SWEPT_FACE",FACE,{"disambiguationData":[OSD([sQuery(id+"F16.wireOp",EDGE,"E44.left")])]});
            var Q21;
            Q21=makeQuery(id+"F17.opExtrude","SWEPT_FACE",FACE,{"disambiguationData":[OSD([sQuery(id+"F16.wireOp",EDGE,"E46.left")])]});
            var Q22;
            Q22=makeQuery(id+"F17.opExtrude","SWEPT_FACE",FACE,{"disambiguationData":[OSD([sQuery(id+"F16.wireOp",EDGE,"f3187e04-98a9-4826-9ade-0eccad066c5c.left")])]});
            var Q23;
            Q23=makeQuery(id+"F17.opExtrude","SWEPT_FACE",FACE,{"disambiguationData":[OSD([sQuery(id+"F16.wireOp",EDGE,"E42.left")])]});
            shell(context, id + "F18", {"entities" : qUnion([Q0, Q1, Q2, Q3, Q4, Q5, Q6, Q7, Q8, Q9, Q10, Q11, Q12, Q13, Q14, Q15, Q16, Q17, Q18, Q19, Q20, Q21, Q22, Q23]), "thickness" : 3.17 * mm});
        }
        {
            var Q0;
            Q0=makeQuery(id+"F14.opShell","OFFSET_FACE",FACE,{"disambiguationData":[OSD([sQuery(id+"F12.wireOp",EDGE,"E27.bottom")])]});
            var sketch = newSketch(context, id + "F19", { "sketchPlane" : qUnion([Q0])});
            skLineSegment(sketch, "E47", {"start": v(-510.8, 1031.88) * mm, "end": v(-536.2, 1031.88) * mm});
            skLineSegment(sketch, "E48", {"start": v(-536.2, 1031.88) * mm, "end": v(-536.2, 1022.35) * mm});
            skLineSegment(sketch, "E49", {"start": v(-536.2, 1022.35) * mm, "end": v(-593.35, 995.7) * mm});
            skLineSegment(sketch, "E50", {"start": v(-593.35, 995.7) * mm, "end": v(-593.35, 944.9) * mm});
            skLineSegment(sketch, "E51", {"start": v(-593.35, 944.9) * mm, "end": v(-536.2, 918.25) * mm});
            skLineSegment(sketch, "E52", {"start": v(-536.2, 918.25) * mm, "end": v(-536.2, 867.45) * mm});
            skLineSegment(sketch, "E53", {"start": v(-536.2, 867.45) * mm, "end": v(-593.35, 840.8) * mm});
            skLineSegment(sketch, "E54", {"start": v(-593.35, 840.8) * mm, "end": v(-593.35, 790) * mm});
            skLineSegment(sketch, "E55", {"start": v(-593.35, 790) * mm, "end": v(-536.2, 763.35) * mm});
            skLineSegment(sketch, "E56", {"start": v(-536.2, 763.35) * mm, "end": v(-536.2, 712.55) * mm});
            skLineSegment(sketch, "E57", {"start": v(-536.2, 712.55) * mm, "end": v(-593.35, 685.9) * mm});
            skLineSegment(sketch, "E58", {"start": v(-593.35, 685.9) * mm, "end": v(-593.35, 635.1) * mm});
            skLineSegment(sketch, "E59", {"start": v(-593.35, 635.1) * mm, "end": v(-536.2, 608.45) * mm});
            skLineSegment(sketch, "E60", {"start": v(-536.2, 608.45) * mm, "end": v(-536.2, 598.93) * mm});
            skLineSegment(sketch, "E61", {"start": v(-536.2, 598.93) * mm, "end": v(-510.8, 598.93) * mm});
            skLineSegment(sketch, "E62", {"start": v(-510.8, 1031.88) * mm, "end": v(-510.8, 598.93) * mm});
            skLineSegment(sketch, "E63", {"start": v(-510.8, 499.62) * mm, "end": v(-536.2, 499.62) * mm});
            skLineSegment(sketch, "E64", {"start": v(-536.2, 499.62) * mm, "end": v(-536.2, 490.1) * mm});
            skLineSegment(sketch, "E65", {"start": v(-536.2, 490.1) * mm, "end": v(-593.35, 463.45) * mm});
            skLineSegment(sketch, "E66", {"start": v(-593.35, 463.45) * mm, "end": v(-593.35, 412.65) * mm});
            skLineSegment(sketch, "E67", {"start": v(-593.35, 412.65) * mm, "end": v(-536.2, 386) * mm});
            skLineSegment(sketch, "E68", {"start": v(-536.2, 386) * mm, "end": v(-536.2, 335.2) * mm});
            skLineSegment(sketch, "E69", {"start": v(-536.2, 335.2) * mm, "end": v(-593.35, 308.55) * mm});
            skLineSegment(sketch, "E70", {"start": v(-593.35, 308.55) * mm, "end": v(-593.35, 257.75) * mm});
            skLineSegment(sketch, "E71", {"start": v(-593.35, 257.75) * mm, "end": v(-536.2, 231.1) * mm});
            skLineSegment(sketch, "E72", {"start": v(-536.2, 231.1) * mm, "end": v(-536.2, 180.3) * mm});
            skLineSegment(sketch, "E73", {"start": v(-536.2, 180.3) * mm, "end": v(-593.35, 153.65) * mm});
            skLineSegment(sketch, "E74", {"start": v(-593.35, 153.65) * mm, "end": v(-593.35, 102.85) * mm});
            skLineSegment(sketch, "E75", {"start": v(-593.35, 102.85) * mm, "end": v(-536.2, 76.2) * mm});
            skLineSegment(sketch, "E76", {"start": v(-536.2, 76.2) * mm, "end": v(-536.2, 66.68) * mm});
            skLineSegment(sketch, "E77", {"start": v(-536.2, 66.68) * mm, "end": v(-510.8, 66.68) * mm});
            skLineSegment(sketch, "E78", {"start": v(-510.8, 499.62) * mm, "end": v(-510.8, 66.68) * mm});
            skSolve(sketch);
        }
        {
            var Q0;
            Q0 = qSketchRegion(id + "F19", true);
            extrude(context, id + "F20", {"entities" : qUnion([Q0]), "endBound" : BoundingType.UP_TO_NEXT, "depth" : 25.4 * mm, "offsetDistance" : 25.4 * mm});
        }
        {
            var Q0;
            Q0=makeQuery(id+"F14.opShell","OFFSET_FACE",FACE,{"disambiguationData":[OSD([sQuery(id+"F12.wireOp",EDGE,"E29.left")])]});
            var sketch = newSketch(context, id + "F21", { "sketchPlane" : qUnion([Q0])});
            skLineSegment(sketch, "E79", {"start": v(-1708.15, 499.62) * mm, "end": v(-1733.55, 499.62) * mm});
            skLineSegment(sketch, "E80", {"start": v(-1733.55, 499.62) * mm, "end": v(-1733.55, 490.1) * mm});
            skLineSegment(sketch, "E81", {"start": v(-1733.55, 490.1) * mm, "end": v(-1790.7, 463.45) * mm});
            skLineSegment(sketch, "E82", {"start": v(-1790.7, 463.45) * mm, "end": v(-1790.7, 412.65) * mm});
            skLineSegment(sketch, "E83", {"start": v(-1790.7, 412.65) * mm, "end": v(-1733.55, 386) * mm});
            skLineSegment(sketch, "E84", {"start": v(-1733.55, 386) * mm, "end": v(-1733.55, 335.2) * mm});
            skLineSegment(sketch, "E85", {"start": v(-1733.55, 335.2) * mm, "end": v(-1790.7, 308.55) * mm});
            skLineSegment(sketch, "E86", {"start": v(-1790.7, 308.55) * mm, "end": v(-1790.7, 257.75) * mm});
            skLineSegment(sketch, "E87", {"start": v(-1790.7, 257.75) * mm, "end": v(-1733.55, 231.1) * mm});
            skLineSegment(sketch, "E88", {"start": v(-1733.55, 231.1) * mm, "end": v(-1733.55, 180.3) * mm});
            skLineSegment(sketch, "E89", {"start": v(-1733.55, 180.3) * mm, "end": v(-1790.7, 153.65) * mm});
            skLineSegment(sketch, "E90", {"start": v(-1790.7, 153.65) * mm, "end": v(-1790.7, 102.85) * mm});
            skLineSegment(sketch, "E91", {"start": v(-1790.7, 102.85) * mm, "end": v(-1733.55, 76.2) * mm});
            skLineSegment(sketch, "E92", {"start": v(-1733.55, 76.2) * mm, "end": v(-1733.55, 66.68) * mm});
            skLineSegment(sketch, "E93", {"start": v(-1733.55, 66.68) * mm, "end": v(-1708.15, 66.68) * mm});
            skLineSegment(sketch, "E94", {"start": v(-1708.15, 499.62) * mm, "end": v(-1708.15, 66.68) * mm});
            skLineSegment(sketch, "E95", {"start": v(-1708.15, 1031.88) * mm, "end": v(-1733.55, 1031.88) * mm});
            skLineSegment(sketch, "E96", {"start": v(-1733.55, 1031.88) * mm, "end": v(-1733.55, 1022.35) * mm});
            skLineSegment(sketch, "E97", {"start": v(-1733.55, 1022.35) * mm, "end": v(-1790.7, 995.7) * mm});
            skLineSegment(sketch, "E98", {"start": v(-1790.7, 995.7) * mm, "end": v(-1790.7, 944.9) * mm});
            skLineSegment(sketch, "E99", {"start": v(-1790.7, 944.9) * mm, "end": v(-1733.55, 918.25) * mm});
            skLineSegment(sketch, "E100", {"start": v(-1733.55, 918.25) * mm, "end": v(-1733.55, 867.45) * mm});
            skLineSegment(sketch, "E101", {"start": v(-1733.55, 867.45) * mm, "end": v(-1790.7, 840.8) * mm});
            skLineSegment(sketch, "E102", {"start": v(-1790.7, 840.8) * mm, "end": v(-1790.7, 790) * mm});
            skLineSegment(sketch, "E103", {"start": v(-1790.7, 790) * mm, "end": v(-1733.55, 763.35) * mm});
            skLineSegment(sketch, "E104", {"start": v(-1733.55, 763.35) * mm, "end": v(-1733.55, 712.55) * mm});
            skLineSegment(sketch, "E105", {"start": v(-1733.55, 712.55) * mm, "end": v(-1790.7, 685.9) * mm});
            skLineSegment(sketch, "E106", {"start": v(-1790.7, 685.9) * mm, "end": v(-1790.7, 635.1) * mm});
            skLineSegment(sketch, "E107", {"start": v(-1790.7, 635.1) * mm, "end": v(-1733.55, 608.45) * mm});
            skLineSegment(sketch, "E108", {"start": v(-1733.55, 608.45) * mm, "end": v(-1733.55, 598.93) * mm});
            skLineSegment(sketch, "E109", {"start": v(-1733.55, 598.93) * mm, "end": v(-1708.15, 598.93) * mm});
            skLineSegment(sketch, "E110", {"start": v(-1708.15, 1031.88) * mm, "end": v(-1708.15, 598.93) * mm});
            skSolve(sketch);
        }
        {
            var Q0;
            Q0 = qSketchRegion(id + "F21", true);
            var Q1;
            Q1=makeQuery(id+"F7.opExtrude","SWEPT_FACE",FACE,{"disambiguationData":[OSD([sQuery(id+"F6.wireOp",EDGE,"E15.left")])]});
            var Q2;
            Q2=makeQuery(id+"F7.opExtrude","SWEPT_FACE",FACE,{"disambiguationData":[OSD([sQuery(id+"F6.wireOp",EDGE,"E16.left")])]});
            extrude(context, id + "F22", {"entities" : qUnion([Q0]), "endBound" : BoundingType.UP_TO_NEXT, "depth" : 25.4 * mm, "endBoundEntityFace" : qUnion([Q1]), "offsetDistance" : 25.4 * mm});
        }
        {
            var Q0;
            Q0=makeQuery(id+"F14.opShell","OFFSET_FACE",FACE,{"disambiguationData":[OSD([sQuery(id+"F12.wireOp",EDGE,"E31.left")])]});
            var sketch = newSketch(context, id + "F23", { "sketchPlane" : qUnion([Q0])});
            skLineSegment(sketch, "E111", {"start": v(-1708.15, 1031.88) * mm, "end": v(-1733.55, 1031.88) * mm});
            skLineSegment(sketch, "E112", {"start": v(-1733.55, 1031.88) * mm, "end": v(-1733.55, 1022.35) * mm});
            skLineSegment(sketch, "E113", {"start": v(-1733.55, 1022.35) * mm, "end": v(-1790.7, 995.7) * mm});
            skLineSegment(sketch, "E114", {"start": v(-1790.7, 995.7) * mm, "end": v(-1790.7, 944.9) * mm});
            skLineSegment(sketch, "E115", {"start": v(-1790.7, 944.9) * mm, "end": v(-1733.55, 918.25) * mm});
            skLineSegment(sketch, "E116", {"start": v(-1733.55, 918.25) * mm, "end": v(-1733.55, 867.45) * mm});
            skLineSegment(sketch, "E117", {"start": v(-1733.55, 867.45) * mm, "end": v(-1790.7, 840.8) * mm});
            skLineSegment(sketch, "E118", {"start": v(-1790.7, 840.8) * mm, "end": v(-1790.7, 790) * mm});
            skLineSegment(sketch, "E119", {"start": v(-1790.7, 790) * mm, "end": v(-1733.55, 763.35) * mm});
            skLineSegment(sketch, "E120", {"start": v(-1733.55, 763.35) * mm, "end": v(-1733.55, 712.55) * mm});
            skLineSegment(sketch, "E121", {"start": v(-1733.55, 712.55) * mm, "end": v(-1790.7, 685.9) * mm});
            skLineSegment(sketch, "E122", {"start": v(-1790.7, 685.9) * mm, "end": v(-1790.7, 635.1) * mm});
            skLineSegment(sketch, "E123", {"start": v(-1790.7, 635.1) * mm, "end": v(-1733.55, 608.45) * mm});
            skLineSegment(sketch, "E124", {"start": v(-1733.55, 608.45) * mm, "end": v(-1733.55, 598.93) * mm});
            skLineSegment(sketch, "E125", {"start": v(-1733.55, 598.93) * mm, "end": v(-1708.15, 598.93) * mm});
            skLineSegment(sketch, "E126", {"start": v(-1708.15, 1031.88) * mm, "end": v(-1708.15, 598.93) * mm});
            skLineSegment(sketch, "E127", {"start": v(-1708.15, 499.62) * mm, "end": v(-1733.55, 499.62) * mm});
            skLineSegment(sketch, "E128", {"start": v(-1733.55, 499.62) * mm, "end": v(-1733.55, 490.1) * mm});
            skLineSegment(sketch, "E129", {"start": v(-1733.55, 490.1) * mm, "end": v(-1790.7, 463.45) * mm});
            skLineSegment(sketch, "E130", {"start": v(-1790.7, 463.45) * mm, "end": v(-1790.7, 412.65) * mm});
            skLineSegment(sketch, "E131", {"start": v(-1790.7, 412.65) * mm, "end": v(-1733.55, 386) * mm});
            skLineSegment(sketch, "E132", {"start": v(-1733.55, 386) * mm, "end": v(-1733.55, 335.2) * mm});
            skLineSegment(sketch, "E133", {"start": v(-1733.55, 335.2) * mm, "end": v(-1790.7, 308.55) * mm});
            skLineSegment(sketch, "E134", {"start": v(-1790.7, 308.55) * mm, "end": v(-1790.7, 257.75) * mm});
            skLineSegment(sketch, "E135", {"start": v(-1790.7, 257.75) * mm, "end": v(-1733.55, 231.1) * mm});
            skLineSegment(sketch, "E136", {"start": v(-1733.55, 231.1) * mm, "end": v(-1733.55, 180.3) * mm});
            skLineSegment(sketch, "E137", {"start": v(-1733.55, 180.3) * mm, "end": v(-1790.7, 153.65) * mm});
            skLineSegment(sketch, "E138", {"start": v(-1790.7, 153.65) * mm, "end": v(-1790.7, 102.85) * mm});
            skLineSegment(sketch, "E139", {"start": v(-1790.7, 102.85) * mm, "end": v(-1733.55, 76.2) * mm});
            skLineSegment(sketch, "E140", {"start": v(-1733.55, 76.2) * mm, "end": v(-1733.55, 66.68) * mm});
            skLineSegment(sketch, "E141", {"start": v(-1733.55, 66.68) * mm, "end": v(-1708.15, 66.68) * mm});
            skLineSegment(sketch, "E142", {"start": v(-1708.15, 499.62) * mm, "end": v(-1708.15, 66.68) * mm});
            skSolve(sketch);
        }
        {
            var Q0;
            Q0 = qSketchRegion(id + "F23", true);
            var Q1;
            Q1=makeQuery(id+"F7.opExtrude","SWEPT_FACE",FACE,{"disambiguationData":[OSD([sQuery(id+"F6.wireOp",EDGE,"E16.left")])]});
            extrude(context, id + "F24", {"entities" : qUnion([Q0]), "endBound" : BoundingType.UP_TO_NEXT, "depth" : 25.4 * mm, "endBoundEntityFace" : qUnion([Q1]), "offsetDistance" : 25.4 * mm});
        }
        {
            var Q0;
            Q0=makeQuery(id+"F14.opShell","OFFSET_FACE",FACE,{"disambiguationData":[OSD([sQuery(id+"F12.wireOp",EDGE,"E33.left")])]});
            var sketch = newSketch(context, id + "F25", { "sketchPlane" : qUnion([Q0])});
            skLineSegment(sketch, "E143", {"start": v(-1708.15, 1031.88) * mm, "end": v(-1733.55, 1031.88) * mm});
            skLineSegment(sketch, "E144", {"start": v(-1733.55, 1031.88) * mm, "end": v(-1733.55, 1022.35) * mm});
            skLineSegment(sketch, "E145", {"start": v(-1733.55, 1022.35) * mm, "end": v(-1790.7, 995.7) * mm});
            skLineSegment(sketch, "E146", {"start": v(-1790.7, 995.7) * mm, "end": v(-1790.7, 944.9) * mm});
            skLineSegment(sketch, "E147", {"start": v(-1790.7, 944.9) * mm, "end": v(-1733.55, 918.25) * mm});
            skLineSegment(sketch, "E148", {"start": v(-1733.55, 918.25) * mm, "end": v(-1733.55, 867.45) * mm});
            skLineSegment(sketch, "E149", {"start": v(-1733.55, 867.45) * mm, "end": v(-1790.7, 840.8) * mm});
            skLineSegment(sketch, "E150", {"start": v(-1790.7, 840.8) * mm, "end": v(-1790.7, 790) * mm});
            skLineSegment(sketch, "E151", {"start": v(-1790.7, 790) * mm, "end": v(-1733.55, 763.35) * mm});
            skLineSegment(sketch, "E152", {"start": v(-1733.55, 763.35) * mm, "end": v(-1733.55, 712.55) * mm});
            skLineSegment(sketch, "E153", {"start": v(-1733.55, 712.55) * mm, "end": v(-1790.7, 685.9) * mm});
            skLineSegment(sketch, "E154", {"start": v(-1790.7, 685.9) * mm, "end": v(-1790.7, 635.1) * mm});
            skLineSegment(sketch, "E155", {"start": v(-1790.7, 635.1) * mm, "end": v(-1733.55, 608.45) * mm});
            skLineSegment(sketch, "E156", {"start": v(-1733.55, 608.45) * mm, "end": v(-1733.55, 598.93) * mm});
            skLineSegment(sketch, "E157", {"start": v(-1733.55, 598.93) * mm, "end": v(-1708.15, 598.93) * mm});
            skLineSegment(sketch, "E158", {"start": v(-1708.15, 1031.88) * mm, "end": v(-1708.15, 598.93) * mm});
            skLineSegment(sketch, "E159", {"start": v(-1708.15, 499.62) * mm, "end": v(-1733.55, 499.62) * mm});
            skLineSegment(sketch, "E160", {"start": v(-1733.55, 499.62) * mm, "end": v(-1733.55, 490.1) * mm});
            skLineSegment(sketch, "E161", {"start": v(-1733.55, 490.1) * mm, "end": v(-1790.7, 463.45) * mm});
            skLineSegment(sketch, "E162", {"start": v(-1790.7, 463.45) * mm, "end": v(-1790.7, 412.65) * mm});
            skLineSegment(sketch, "E163", {"start": v(-1790.7, 412.65) * mm, "end": v(-1733.55, 386) * mm});
            skLineSegment(sketch, "E164", {"start": v(-1733.55, 386) * mm, "end": v(-1733.55, 335.2) * mm});
            skLineSegment(sketch, "E165", {"start": v(-1733.55, 335.2) * mm, "end": v(-1790.7, 308.55) * mm});
            skLineSegment(sketch, "E166", {"start": v(-1790.7, 308.55) * mm, "end": v(-1790.7, 257.75) * mm});
            skLineSegment(sketch, "E167", {"start": v(-1790.7, 257.75) * mm, "end": v(-1733.55, 231.1) * mm});
            skLineSegment(sketch, "E168", {"start": v(-1733.55, 231.1) * mm, "end": v(-1733.55, 180.3) * mm});
            skLineSegment(sketch, "E169", {"start": v(-1733.55, 180.3) * mm, "end": v(-1790.7, 153.65) * mm});
            skLineSegment(sketch, "E170", {"start": v(-1790.7, 153.65) * mm, "end": v(-1790.7, 102.85) * mm});
            skLineSegment(sketch, "E171", {"start": v(-1790.7, 102.85) * mm, "end": v(-1733.55, 76.2) * mm});
            skLineSegment(sketch, "E172", {"start": v(-1733.55, 76.2) * mm, "end": v(-1733.55, 66.68) * mm});
            skLineSegment(sketch, "E173", {"start": v(-1733.55, 66.68) * mm, "end": v(-1708.15, 66.68) * mm});
            skLineSegment(sketch, "E174", {"start": v(-1708.15, 499.62) * mm, "end": v(-1708.15, 66.68) * mm});
            skSolve(sketch);
        }
        {
            var Q0;
            Q0 = qSketchRegion(id + "F25", true);
            var Q1;
            Q1=makeQuery(id+"F7.opExtrude","SWEPT_FACE",FACE,{"disambiguationData":[OSD([sQuery(id+"F6.wireOp",EDGE,"E17.left")])]});
            extrude(context, id + "F26", {"entities" : qUnion([Q0]), "endBound" : BoundingType.UP_TO_NEXT, "depth" : 25.4 * mm, "endBoundEntityFace" : qUnion([Q1]), "offsetDistance" : 25.4 * mm});
        }
        {
            var Q0;
            Q0=makeQuery(id+"F14.opShell","OFFSET_FACE",FACE,{"disambiguationData":[OSD([sQuery(id+"F12.wireOp",EDGE,"E35.left")])]});
            var sketch = newSketch(context, id + "F27", { "sketchPlane" : qUnion([Q0])});
            skLineSegment(sketch, "E175", {"start": v(-1708.15, 1031.88) * mm, "end": v(-1733.55, 1031.88) * mm});
            skLineSegment(sketch, "E176", {"start": v(-1733.55, 1031.88) * mm, "end": v(-1733.55, 1022.35) * mm});
            skLineSegment(sketch, "E177", {"start": v(-1733.55, 1022.35) * mm, "end": v(-1790.7, 995.7) * mm});
            skLineSegment(sketch, "E178", {"start": v(-1790.7, 995.7) * mm, "end": v(-1790.7, 944.9) * mm});
            skLineSegment(sketch, "E179", {"start": v(-1790.7, 944.9) * mm, "end": v(-1733.55, 918.25) * mm});
            skLineSegment(sketch, "E180", {"start": v(-1733.55, 918.25) * mm, "end": v(-1733.55, 867.45) * mm});
            skLineSegment(sketch, "E181", {"start": v(-1733.55, 867.45) * mm, "end": v(-1790.7, 840.8) * mm});
            skLineSegment(sketch, "E182", {"start": v(-1790.7, 840.8) * mm, "end": v(-1790.7, 790) * mm});
            skLineSegment(sketch, "E183", {"start": v(-1790.7, 790) * mm, "end": v(-1733.55, 763.35) * mm});
            skLineSegment(sketch, "E184", {"start": v(-1733.55, 763.35) * mm, "end": v(-1733.55, 712.55) * mm});
            skLineSegment(sketch, "E185", {"start": v(-1733.55, 712.55) * mm, "end": v(-1790.7, 685.9) * mm});
            skLineSegment(sketch, "E186", {"start": v(-1790.7, 685.9) * mm, "end": v(-1790.7, 635.1) * mm});
            skLineSegment(sketch, "E187", {"start": v(-1790.7, 635.1) * mm, "end": v(-1733.55, 608.45) * mm});
            skLineSegment(sketch, "E188", {"start": v(-1733.55, 608.45) * mm, "end": v(-1733.55, 598.93) * mm});
            skLineSegment(sketch, "E189", {"start": v(-1733.55, 598.93) * mm, "end": v(-1708.15, 598.93) * mm});
            skLineSegment(sketch, "E190", {"start": v(-1708.15, 1031.88) * mm, "end": v(-1708.15, 598.93) * mm});
            skLineSegment(sketch, "E191", {"start": v(-1708.15, 499.62) * mm, "end": v(-1733.55, 499.62) * mm});
            skLineSegment(sketch, "E192", {"start": v(-1733.55, 499.62) * mm, "end": v(-1733.55, 490.1) * mm});
            skLineSegment(sketch, "E193", {"start": v(-1733.55, 490.1) * mm, "end": v(-1790.7, 463.45) * mm});
            skLineSegment(sketch, "E194", {"start": v(-1790.7, 463.45) * mm, "end": v(-1790.7, 412.65) * mm});
            skLineSegment(sketch, "E195", {"start": v(-1790.7, 412.65) * mm, "end": v(-1733.55, 386) * mm});
            skLineSegment(sketch, "E196", {"start": v(-1733.55, 386) * mm, "end": v(-1733.55, 335.2) * mm});
            skLineSegment(sketch, "E197", {"start": v(-1733.55, 335.2) * mm, "end": v(-1790.7, 308.55) * mm});
            skLineSegment(sketch, "E198", {"start": v(-1790.7, 308.55) * mm, "end": v(-1790.7, 257.75) * mm});
            skLineSegment(sketch, "E199", {"start": v(-1790.7, 257.75) * mm, "end": v(-1733.55, 231.1) * mm});
            skLineSegment(sketch, "E200", {"start": v(-1733.55, 231.1) * mm, "end": v(-1733.55, 180.3) * mm});
            skLineSegment(sketch, "E201", {"start": v(-1733.55, 180.3) * mm, "end": v(-1790.7, 153.65) * mm});
            skLineSegment(sketch, "E202", {"start": v(-1790.7, 153.65) * mm, "end": v(-1790.7, 102.85) * mm});
            skLineSegment(sketch, "E203", {"start": v(-1790.7, 102.85) * mm, "end": v(-1733.55, 76.2) * mm});
            skLineSegment(sketch, "E204", {"start": v(-1733.55, 76.2) * mm, "end": v(-1733.55, 66.68) * mm});
            skLineSegment(sketch, "E205", {"start": v(-1733.55, 66.68) * mm, "end": v(-1708.15, 66.68) * mm});
            skLineSegment(sketch, "E206", {"start": v(-1708.15, 499.62) * mm, "end": v(-1708.15, 66.68) * mm});
            skSolve(sketch);
        }
        {
            var Q0;
            Q0 = qSketchRegion(id + "F27", true);
            var Q1;
            Q1=makeQuery(id+"F7.opExtrude","SWEPT_FACE",FACE,{"disambiguationData":[OSD([sQuery(id+"F6.wireOp",EDGE,"E18.left")])]});
            extrude(context, id + "F28", {"entities" : qUnion([Q0]), "endBound" : BoundingType.UP_TO_NEXT, "depth" : 25.4 * mm, "endBoundEntityFace" : qUnion([Q1]), "offsetDistance" : 25.4 * mm});
        }
        {
            var Q0;
            Q0=makeQuery(id+"F20.opExtrude","SWEPT_FACE",FACE,{"disambiguationData":[OSD([sQuery(id+"F19.wireOp",EDGE,"E62")])]});
            var Q1;
            Q1=makeQuery(id+"F20.opExtrude","SWEPT_FACE",FACE,{"disambiguationData":[OSD([sQuery(id+"F19.wireOp",EDGE,"E78")])]});
            var Q2;
            Q2=makeQuery(id+"F22.opExtrude","SWEPT_FACE",FACE,{"disambiguationData":[OSD([sQuery(id+"F21.wireOp",EDGE,"E110")])]});
            var Q3;
            Q3=makeQuery(id+"F22.opExtrude","SWEPT_FACE",FACE,{"disambiguationData":[OSD([sQuery(id+"F21.wireOp",EDGE,"E94")])]});
            var Q4;
            Q4=makeQuery(id+"F24.opExtrude","SWEPT_FACE",FACE,{"disambiguationData":[OSD([sQuery(id+"F23.wireOp",EDGE,"E142")])]});
            var Q5;
            Q5=makeQuery(id+"F24.opExtrude","SWEPT_FACE",FACE,{"disambiguationData":[OSD([sQuery(id+"F23.wireOp",EDGE,"E126")])]});
            var Q6;
            Q6=makeQuery(id+"F26.opExtrude","SWEPT_FACE",FACE,{"disambiguationData":[OSD([sQuery(id+"F25.wireOp",EDGE,"E158")])]});
            var Q7;
            Q7=makeQuery(id+"F26.opExtrude","SWEPT_FACE",FACE,{"disambiguationData":[OSD([sQuery(id+"F25.wireOp",EDGE,"E174")])]});
            var Q8;
            Q8=makeQuery(id+"F28.opExtrude","SWEPT_FACE",FACE,{"disambiguationData":[OSD([sQuery(id+"F27.wireOp",EDGE,"E206")])]});
            var Q9;
            Q9=makeQuery(id+"F28.opExtrude","SWEPT_FACE",FACE,{"disambiguationData":[OSD([sQuery(id+"F27.wireOp",EDGE,"E190")])]});
            shell(context, id + "F29", {"entities" : qUnion([Q0, Q1, Q2, Q3, Q4, Q5, Q6, Q7, Q8, Q9]), "thickness" : 3.17 * mm});
        }
        {
            var Q0;
            Q0=makeQuery(id+"F13.opExtrude","SWEPT_FACE",FACE,{"disambiguationData":[OSD([sQuery(id+"F12.wireOp",EDGE,"E27.left")])]});
            var sketch = newSketch(context, id + "F30", { "sketchPlane" : qUnion([Q0])});
            skLineSegment(sketch, "E207.bottom", {"start": v(577.85, 1047.75) * mm, "end": v(485.77, 1047.75) * mm});
            skLineSegment(sketch, "E207.top", {"start": v(577.85, 812.8) * mm, "end": v(485.77, 812.8) * mm});
            skLineSegment(sketch, "E207.left", {"start": v(577.85, 1047.75) * mm, "end": v(577.85, 812.8) * mm});
            skLineSegment(sketch, "E207.right", {"start": v(485.77, 1047.75) * mm, "end": v(485.77, 812.8) * mm});
            skLineSegment(sketch, "E208.bottom", {"start": v(577.85, 515.5) * mm, "end": v(485.78, 515.5) * mm});
            skLineSegment(sketch, "E208.top", {"start": v(577.85, 280.54) * mm, "end": v(485.78, 280.54) * mm});
            skLineSegment(sketch, "E208.left", {"start": v(577.85, 515.5) * mm, "end": v(577.85, 280.54) * mm});
            skLineSegment(sketch, "E208.right", {"start": v(485.78, 515.5) * mm, "end": v(485.78, 280.54) * mm});
            skSolve(sketch);
        }
        {
            var Q0;
            Q0 = qSketchRegion(id + "F30", true);
            extrude(context, id + "F31", {"entities" : qUnion([Q0]), "operationType" : NewBodyOperationType.REMOVE, "oppositeDirection" : true, "depth" : 3.17 * mm, "offsetDistance" : 25.4 * mm});
        }
        {
            var Q0;
            Q0=makeQuery(id+"F13.opExtrude","SWEPT_FACE",FACE,{"disambiguationData":[OSD([sQuery(id+"F12.wireOp",EDGE,"E29.top")])]});
            var sketch = newSketch(context, id + "F32", { "sketchPlane" : qUnion([Q0])});
            skLineSegment(sketch, "E209.bottom", {"start": v(-409.2, 1047.75) * mm, "end": v(-501.27, 1047.75) * mm});
            skLineSegment(sketch, "E209.top", {"start": v(-409.2, 812.8) * mm, "end": v(-501.27, 812.8) * mm});
            skLineSegment(sketch, "E209.left", {"start": v(-409.2, 1047.75) * mm, "end": v(-409.2, 812.8) * mm});
            skLineSegment(sketch, "E209.right", {"start": v(-501.27, 1047.75) * mm, "end": v(-501.27, 812.8) * mm});
            skLineSegment(sketch, "E210.bottom", {"start": v(-409.2, 515.5) * mm, "end": v(-501.27, 515.5) * mm});
            skLineSegment(sketch, "E210.top", {"start": v(-409.2, 280.54) * mm, "end": v(-501.27, 280.54) * mm});
            skLineSegment(sketch, "E210.left", {"start": v(-409.2, 515.5) * mm, "end": v(-409.2, 280.54) * mm});
            skLineSegment(sketch, "E210.right", {"start": v(-501.27, 515.5) * mm, "end": v(-501.27, 280.54) * mm});
            skLineSegment(sketch, "E211.bottom", {"start": v(2334, 1047.75) * mm, "end": v(2241.93, 1047.75) * mm});
            skLineSegment(sketch, "E211.top", {"start": v(2334, 812.8) * mm, "end": v(2241.93, 812.8) * mm});
            skLineSegment(sketch, "E211.left", {"start": v(2334, 1047.75) * mm, "end": v(2334, 812.8) * mm});
            skLineSegment(sketch, "E211.right", {"start": v(2241.93, 1047.75) * mm, "end": v(2241.93, 812.8) * mm});
            skLineSegment(sketch, "E212.bottom", {"start": v(2334, 515.5) * mm, "end": v(2241.93, 515.5) * mm});
            skLineSegment(sketch, "E212.top", {"start": v(2334, 280.54) * mm, "end": v(2241.93, 280.54) * mm});
            skLineSegment(sketch, "E212.left", {"start": v(2334, 515.5) * mm, "end": v(2334, 280.54) * mm});
            skLineSegment(sketch, "E212.right", {"start": v(2241.93, 515.5) * mm, "end": v(2241.93, 280.54) * mm});
            skLineSegment(sketch, "E213.bottom", {"start": v(5077.2, 1047.75) * mm, "end": v(4985.13, 1047.75) * mm});
            skLineSegment(sketch, "E213.top", {"start": v(5077.2, 812.8) * mm, "end": v(4985.13, 812.8) * mm});
            skLineSegment(sketch, "E213.left", {"start": v(5077.2, 1047.75) * mm, "end": v(5077.2, 812.8) * mm});
            skLineSegment(sketch, "E213.right", {"start": v(4985.13, 1047.75) * mm, "end": v(4985.13, 812.8) * mm});
            skLineSegment(sketch, "E214.bottom", {"start": v(5077.2, 515.5) * mm, "end": v(4985.13, 515.5) * mm});
            skLineSegment(sketch, "E214.top", {"start": v(5077.2, 280.54) * mm, "end": v(4985.13, 280.54) * mm});
            skLineSegment(sketch, "E214.left", {"start": v(5077.2, 515.5) * mm, "end": v(5077.2, 280.54) * mm});
            skLineSegment(sketch, "E214.right", {"start": v(4985.13, 515.5) * mm, "end": v(4985.13, 280.54) * mm});
            skLineSegment(sketch, "E215.bottom", {"start": v(7820.4, 1047.75) * mm, "end": v(7728.33, 1047.75) * mm});
            skLineSegment(sketch, "E215.top", {"start": v(7820.4, 812.8) * mm, "end": v(7728.33, 812.8) * mm});
            skLineSegment(sketch, "E215.left", {"start": v(7820.4, 1047.75) * mm, "end": v(7820.4, 812.8) * mm});
            skLineSegment(sketch, "E215.right", {"start": v(7728.33, 1047.75) * mm, "end": v(7728.33, 812.8) * mm});
            skLineSegment(sketch, "E216.bottom", {"start": v(7820.4, 515.5) * mm, "end": v(7728.33, 515.5) * mm});
            skLineSegment(sketch, "E216.top", {"start": v(7820.4, 280.54) * mm, "end": v(7728.33, 280.54) * mm});
            skLineSegment(sketch, "E216.left", {"start": v(7820.4, 515.5) * mm, "end": v(7820.4, 280.54) * mm});
            skLineSegment(sketch, "E216.right", {"start": v(7728.33, 515.5) * mm, "end": v(7728.33, 280.54) * mm});
            skSolve(sketch);
        }
        {
            var Q0;
            Q0 = qSketchRegion(id + "F32", true);
            extrude(context, id + "F33", {"entities" : qUnion([Q0]), "operationType" : NewBodyOperationType.REMOVE, "oppositeDirection" : true, "depth" : 3.17 * mm, "offsetDistance" : 25.4 * mm});
        }
        {
            var Q0;
            Q0=makeQuery(id+"F7.opExtrude","SWEPT_FACE",FACE,{"disambiguationData":[OSD([sQuery(id+"F6.wireOp",EDGE,"E18.right")])]});
            var sketch = newSketch(context, id + "F34", { "sketchPlane" : qUnion([Q0])});
            skLineSegment(sketch, "E217.bottom", {"start": v(-1803.4, 1031.88) * mm, "end": v(-1701.8, 1031.88) * mm});
            skLineSegment(sketch, "E217.top", {"start": v(-1803.4, 727.08) * mm, "end": v(-1701.8, 727.08) * mm});
            skLineSegment(sketch, "E217.left", {"start": v(-1803.4, 1031.88) * mm, "end": v(-1803.4, 727.08) * mm});
            skLineSegment(sketch, "E217.right", {"start": v(-1701.8, 1031.88) * mm, "end": v(-1701.8, 727.08) * mm});
            skLineSegment(sketch, "E218.bottom", {"start": v(-1803.4, 371.48) * mm, "end": v(-1701.8, 371.48) * mm});
            skLineSegment(sketch, "E218.top", {"start": v(-1803.4, 66.68) * mm, "end": v(-1701.8, 66.68) * mm});
            skLineSegment(sketch, "E218.left", {"start": v(-1803.4, 371.48) * mm, "end": v(-1803.4, 66.68) * mm});
            skLineSegment(sketch, "E218.right", {"start": v(-1701.8, 371.48) * mm, "end": v(-1701.8, 66.68) * mm});
            skSolve(sketch);
        }
        {
            var Q0;
            Q0 = qSketchRegion(id + "F34", true);
            extrude(context, id + "F35", {"entities" : qUnion([Q0]), "depth" : 3.17 * mm, "offsetDistance" : 25.4 * mm});
        }
        {
            var Q0;
            Q0=makeQuery(id+"F35.opExtrude","CAP_FACE",FACE,{"disambiguationData":[OSD([sQuery(id+"F34.wireOp",EDGE,"E217.bottom"),sQuery(id+"F34.wireOp",EDGE,"E217.top"),sQuery(id+"F34.wireOp",EDGE,"E217.left"),sQuery(id+"F34.wireOp",EDGE,"E217.right")])],"isStart":false});
            var sketch = newSketch(context, id + "F36", { "sketchPlane" : qUnion([Q0])});
            skCircle(sketch, "E219", {"center": v(-1752.6, 879.48) * mm, "radius": 19.05 * mm});
            skPoint(sketch, "E219.centerSnap0", {"position": v(-1752.6, 727.08) * mm});
            skPoint(sketch, "E219.centerSnap1", {"position": v(-1701.8, 879.48) * mm});
            skCircle(sketch, "E220", {"center": v(-1752.6, 219.08) * mm, "radius": 19.05 * mm});
            skSolve(sketch);
        }
        {
            var Q0;
            Q0 = qSketchRegion(id + "F36", true);
            extrude(context, id + "F37", {"entities" : qUnion([Q0]), "operationType" : NewBodyOperationType.ADD, "depth" : 6.35 * mm, "offsetDistance" : 25.4 * mm});
        }
        {
            var Q0;
            Q0=makeQuery(id+"F37.opExtrude","CAP_FACE",FACE,{"disambiguationData":[OSD([sQuery(id+"F36.wireOp",EDGE,"E219")])],"isStart":false});
            var sketch = newSketch(context, id + "F38", { "sketchPlane" : qUnion([Q0])});
            skLineSegment(sketch, "E221.bottom", {"start": v(-1778, 930.28) * mm, "end": v(-1727.2, 930.28) * mm});
            skLineSegment(sketch, "E221.top", {"start": v(-1778, 828.68) * mm, "end": v(-1727.2, 828.68) * mm});
            skLineSegment(sketch, "E221.left", {"start": v(-1778, 930.28) * mm, "end": v(-1778, 828.68) * mm});
            skLineSegment(sketch, "E221.right", {"start": v(-1727.2, 930.28) * mm, "end": v(-1727.2, 828.68) * mm});
            skLineSegment(sketch, "E222.bottom", {"start": v(-1778, 269.88) * mm, "end": v(-1727.2, 269.88) * mm});
            skLineSegment(sketch, "E222.top", {"start": v(-1778, 168.28) * mm, "end": v(-1727.2, 168.28) * mm});
            skLineSegment(sketch, "E222.left", {"start": v(-1778, 269.88) * mm, "end": v(-1778, 168.28) * mm});
            skLineSegment(sketch, "E222.right", {"start": v(-1727.2, 269.88) * mm, "end": v(-1727.2, 168.28) * mm});
            skSolve(sketch);
        }
        {
            var Q0;
            Q0 = qSketchRegion(id + "F38", true);
            extrude(context, id + "F39", {"entities" : qUnion([Q0]), "depth" : 44.45 * mm, "offsetDistance" : 25.4 * mm});
        }
        {
            var Q0;
            Q0=makeQuery(id+"F39.opExtrude","CAP_FACE",FACE,{"disambiguationData":[OSD([sQuery(id+"F38.wireOp",EDGE,"E221.bottom"),sQuery(id+"F38.wireOp",EDGE,"E221.top"),sQuery(id+"F38.wireOp",EDGE,"E221.left"),sQuery(id+"F38.wireOp",EDGE,"E221.right")])],"isStart":false});
            var Q1;
            Q1=makeQuery(id+"F39.opExtrude","CAP_FACE",FACE,{"disambiguationData":[OSD([sQuery(id+"F38.wireOp",EDGE,"E222.bottom"),sQuery(id+"F38.wireOp",EDGE,"E222.top"),sQuery(id+"F38.wireOp",EDGE,"E222.left"),sQuery(id+"F38.wireOp",EDGE,"E222.right")])],"isStart":false});
            var Q2;
            Q2=makeQuery(id+"F39.opExtrude","SWEPT_FACE",FACE,{"disambiguationData":[OSD([sQuery(id+"F38.wireOp",EDGE,"E222.bottom")])]});
            var Q3;
            Q3=makeQuery(id+"F39.opExtrude","SWEPT_FACE",FACE,{"disambiguationData":[OSD([sQuery(id+"F38.wireOp",EDGE,"E221.bottom")])]});
            var Q4;
            Q4=makeQuery(id+"F39.opExtrude","SWEPT_FACE",FACE,{"disambiguationData":[OSD([sQuery(id+"F38.wireOp",EDGE,"E222.top")])]});
            var Q5;
            Q5=makeQuery(id+"F39.opExtrude","SWEPT_FACE",FACE,{"disambiguationData":[OSD([sQuery(id+"F38.wireOp",EDGE,"E221.top")])]});
            shell(context, id + "F40", {"entities" : qUnion([Q0, Q1, Q2, Q3, Q4, Q5]), "thickness" : 2.54 * mm});
        }
        {
            var Q0;
            {var subQ0=sQuery(id+"F38.wireOp",EDGE,"E221.right");var subQ1=sQuery(id+"F38.wireOp",EDGE,"E221.left");var subQ2=sQuery(id+"F38.wireOp",EDGE,"E221.top");var subQ3=sQuery(id+"F38.wireOp",EDGE,"E221.bottom");Q0=makeQuery(id+"F40.opShell","OFFSET_FACE",FACE,{"disambiguationData":[OSD([subQ3,subQ2,subQ1,subQ0]),TDD([makeQuery(id+"F39.opExtrude","CAP_FACE",FACE,{"disambiguationData":[OSD([subQ3,subQ2,subQ1,subQ0])],"isStart":true})])]});}
            cPlane(context, id + "F41", {"entities" : qUnion([Q0]), "cplaneType" : CPlaneType.OFFSET, "offset" : 3.17 * mm, "width" : 152.4 * mm, "height" : 152.4 * mm});
        }
        {
            var Q0;
            Q0=qCreatedBy(id+"F41.planeOp",FACE);
            var sketch = newSketch(context, id + "F42", { "sketchPlane" : qUnion([Q0])});
            skLineSegment(sketch, "E223.bottom", {"start": v(-1772.29, 935.36) * mm, "end": v(-1732.92, 935.36) * mm});
            skLineSegment(sketch, "E223.top", {"start": v(-1772.29, 823.6) * mm, "end": v(-1732.92, 823.6) * mm});
            skLineSegment(sketch, "E223.left", {"start": v(-1772.29, 935.36) * mm, "end": v(-1772.29, 823.6) * mm});
            skLineSegment(sketch, "E223.right", {"start": v(-1732.92, 935.36) * mm, "end": v(-1732.92, 823.6) * mm});
            skLineSegment(sketch, "E224.bottom", {"start": v(-1772.29, 274.96) * mm, "end": v(-1732.92, 274.96) * mm});
            skLineSegment(sketch, "E224.top", {"start": v(-1772.29, 163.2) * mm, "end": v(-1732.92, 163.2) * mm});
            skLineSegment(sketch, "E224.left", {"start": v(-1772.29, 274.96) * mm, "end": v(-1772.29, 163.2) * mm});
            skLineSegment(sketch, "E224.right", {"start": v(-1732.92, 274.96) * mm, "end": v(-1732.92, 163.2) * mm});
            skSolve(sketch);
        }
        {
            var Q0;
            Q0 = qSketchRegion(id + "F42", true);
            extrude(context, id + "F43", {"entities" : qUnion([Q0]), "depth" : 44.45 * mm, "offsetDistance" : 25.4 * mm});
        }
        {
            var Q0;
            Q0=makeQuery(id+"F43.opExtrude","SWEPT_FACE",FACE,{"disambiguationData":[OSD([sQuery(id+"F42.wireOp",EDGE,"E223.left")])]});
            var Q1;
            Q1=makeQuery(id+"F43.opExtrude","CAP_FACE",FACE,{"disambiguationData":[OSD([sQuery(id+"F42.wireOp",EDGE,"E223.bottom"),sQuery(id+"F42.wireOp",EDGE,"E223.top"),sQuery(id+"F42.wireOp",EDGE,"E223.left"),sQuery(id+"F42.wireOp",EDGE,"E223.right")])],"isStart":true});
            var Q2;
            Q2=makeQuery(id+"F43.opExtrude","CAP_FACE",FACE,{"disambiguationData":[OSD([sQuery(id+"F42.wireOp",EDGE,"E224.bottom"),sQuery(id+"F42.wireOp",EDGE,"E224.top"),sQuery(id+"F42.wireOp",EDGE,"E224.left"),sQuery(id+"F42.wireOp",EDGE,"E224.right")])],"isStart":true});
            var Q3;
            Q3=makeQuery(id+"F43.opExtrude","SWEPT_FACE",FACE,{"disambiguationData":[OSD([sQuery(id+"F42.wireOp",EDGE,"E224.left")])]});
            var Q4;
            Q4=makeQuery(id+"F43.opExtrude","SWEPT_FACE",FACE,{"disambiguationData":[OSD([sQuery(id+"F42.wireOp",EDGE,"E223.right")])]});
            var Q5;
            Q5=makeQuery(id+"F43.opExtrude","SWEPT_FACE",FACE,{"disambiguationData":[OSD([sQuery(id+"F42.wireOp",EDGE,"E224.right")])]});
            shell(context, id + "F44", {"entities" : qUnion([Q0, Q1, Q2, Q3, Q4, Q5]), "thickness" : 2.54 * mm});
        }
        {
            var Q0;
            Q0=makeQuery(id+"F43.opExtrude","SWEPT_FACE",FACE,{"disambiguationData":[OSD([sQuery(id+"F42.wireOp",EDGE,"E223.bottom")])]});
            var sketch = newSketch(context, id + "F45", { "sketchPlane" : qUnion([Q0])});
            skCircle(sketch, "E225", {"center": v(10201.02, -1751.96) * mm, "radius": 6.99 * mm});
            skSolve(sketch);
        }
        {
            var Q0;
            Q0 = qSketchRegion(id + "F45", true);
            extrude(context, id + "F46", {"entities" : qUnion([Q0]), "operationType" : NewBodyOperationType.ADD, "depth" : 4.44 * mm, "offsetDistance" : 25.4 * mm});
        }
        {
            var Q0;
            Q0 = qSketchRegion(id + "F45", true);
            extrude(context, id + "F47", {"entities" : qUnion([Q0]), "operationType" : NewBodyOperationType.ADD, "oppositeDirection" : true, "depth" : 114.3 * mm, "offsetDistance" : 25.4 * mm});
        }
        {
            var Q0;
            Q0=makeQuery(id+"F43.opExtrude","SWEPT_FACE",FACE,{"disambiguationData":[OSD([sQuery(id+"F42.wireOp",EDGE,"E224.bottom")])]});
            var sketch = newSketch(context, id + "F48", { "sketchPlane" : qUnion([Q0])});
            skCircle(sketch, "E226", {"center": v(10201.02, -1751.96) * mm, "radius": 6.99 * mm});
            skSolve(sketch);
        }
        {
            var Q0;
            Q0 = qSketchRegion(id + "F48", true);
            extrude(context, id + "F49", {"entities" : qUnion([Q0]), "operationType" : NewBodyOperationType.ADD, "depth" : 4.44 * mm, "offsetDistance" : 25.4 * mm});
        }
        {
            var Q0;
            Q0 = qSketchRegion(id + "F48", true);
            extrude(context, id + "F50", {"entities" : qUnion([Q0]), "operationType" : NewBodyOperationType.ADD, "oppositeDirection" : true, "depth" : 114.3 * mm, "offsetDistance" : 25.4 * mm});
        }
        {
            var Q0;
            Q0=makeQuery(id+"F43.opExtrude","CAP_FACE",FACE,{"disambiguationData":[OSD([sQuery(id+"F42.wireOp",EDGE,"E223.bottom"),sQuery(id+"F42.wireOp",EDGE,"E223.top"),sQuery(id+"F42.wireOp",EDGE,"E223.left"),sQuery(id+"F42.wireOp",EDGE,"E223.right")])],"isStart":false});
            var sketch = newSketch(context, id + "F51", { "sketchPlane" : qUnion([Q0])});
            skLineSegment(sketch, "E227.bottom", {"start": v(-1803.4, 1019.18) * mm, "end": v(-1714.5, 1019.18) * mm});
            skLineSegment(sketch, "E227.top", {"start": v(-1803.4, 53.98) * mm, "end": v(-1714.5, 53.98) * mm});
            skLineSegment(sketch, "E227.left", {"start": v(-1803.4, 1019.18) * mm, "end": v(-1803.4, 53.97) * mm});
            skLineSegment(sketch, "E227.right", {"start": v(-1714.5, 1019.18) * mm, "end": v(-1714.5, 53.97) * mm});
            skSolve(sketch);
        }
        {
            var Q0;
            Q0 = qSketchRegion(id + "F51", true);
            extrude(context, id + "F52", {"entities" : qUnion([Q0]), "depth" : 31.75 * mm, "offsetDistance" : 25.4 * mm});
        }
        {
            var Q0;
            Q0=makeQuery(id+"F52.opExtrude","CAP_FACE",FACE,{"disambiguationData":[OSD([sQuery(id+"F51.wireOp",EDGE,"E227.bottom"),sQuery(id+"F51.wireOp",EDGE,"E227.top"),sQuery(id+"F51.wireOp",EDGE,"E227.left"),sQuery(id+"F51.wireOp",EDGE,"E227.right")])],"isStart":false});
            var sketch = newSketch(context, id + "F53", { "sketchPlane" : qUnion([Q0])});
            skLineSegment(sketch, "E228.bottom", {"start": v(-1717.67, 1019.18) * mm, "end": v(-1730.37, 1019.18) * mm});
            skLineSegment(sketch, "E228.top", {"start": v(-1717.67, 663.58) * mm, "end": v(-1730.37, 663.58) * mm});
            skLineSegment(sketch, "E228.left", {"start": v(-1717.67, 1019.18) * mm, "end": v(-1717.67, 663.58) * mm});
            skLineSegment(sketch, "E228.right", {"start": v(-1730.37, 1019.18) * mm, "end": v(-1730.37, 987.43) * mm});
            skLineSegment(sketch, "E229.bottom", {"start": v(-1736.72, 981.08) * mm, "end": v(-1784.35, 981.08) * mm});
            skLineSegment(sketch, "E229.top", {"start": v(-1736.72, 942.98) * mm, "end": v(-1784.35, 942.98) * mm});
            skLineSegment(sketch, "E229.right", {"start": v(-1790.7, 974.73) * mm, "end": v(-1790.7, 949.33) * mm});
            skLineSegment(sketch, "E230.bottom", {"start": v(-1784.35, 866.78) * mm, "end": v(-1736.72, 866.78) * mm});
            skLineSegment(sketch, "E230.top", {"start": v(-1784.35, 828.68) * mm, "end": v(-1736.72, 828.68) * mm});
            skLineSegment(sketch, "E230.left", {"start": v(-1790.7, 860.43) * mm, "end": v(-1790.7, 835.02) * mm});
            skLineSegment(sketch, "E231.bottom", {"start": v(-1736.72, 714.38) * mm, "end": v(-1784.35, 714.38) * mm});
            skLineSegment(sketch, "E231.top", {"start": v(-1736.72, 752.48) * mm, "end": v(-1784.35, 752.48) * mm});
            skLineSegment(sketch, "E231.right", {"start": v(-1790.7, 720.72) * mm, "end": v(-1790.7, 746.12) * mm});
            skLineSegment(sketch, "E232.trimOffspring", {"start": v(-1730.37, 936.62) * mm, "end": v(-1730.37, 873.13) * mm});
            skLineSegment(sketch, "E233.trimOffspring", {"start": v(-1730.37, 822.32) * mm, "end": v(-1730.37, 758.83) * mm});
            skLineSegment(sketch, "E234.trimOffspring", {"start": v(-1730.37, 708.02) * mm, "end": v(-1730.37, 663.58) * mm});
            skPoint(sketch, "E235.visualSharp", {"position": v(-1730.37, 981.08) * mm});
            skArc(sketch, "E235.filletArc", {"start": v(-1736.72, 981.08) * mm, "mid": v(-1732.23, 982.93) * mm, "end": v(-1730.37, 987.43) * mm});
            skPoint(sketch, "E236.visualSharp", {"position": v(-1790.7, 981.08) * mm});
            skArc(sketch, "E236.filletArc", {"start": v(-1784.35, 981.08) * mm, "mid": v(-1788.84, 979.22) * mm, "end": v(-1790.7, 974.73) * mm});
            skPoint(sketch, "E237.visualSharp", {"position": v(-1730.37, 942.98) * mm});
            skArc(sketch, "E237.filletArc", {"start": v(-1730.37, 936.62) * mm, "mid": v(-1732.23, 941.12) * mm, "end": v(-1736.72, 942.98) * mm});
            skPoint(sketch, "E238.visualSharp", {"position": v(-1790.7, 942.98) * mm});
            skArc(sketch, "E238.filletArc", {"start": v(-1790.7, 949.33) * mm, "mid": v(-1788.84, 944.83) * mm, "end": v(-1784.35, 942.97) * mm});
            skPoint(sketch, "E239.visualSharp", {"position": v(-1790.7, 866.78) * mm});
            skArc(sketch, "E239.filletArc", {"start": v(-1784.35, 866.78) * mm, "mid": v(-1788.84, 864.92) * mm, "end": v(-1790.7, 860.43) * mm});
            skPoint(sketch, "E240.visualSharp", {"position": v(-1730.37, 866.78) * mm});
            skArc(sketch, "E240.filletArc", {"start": v(-1736.72, 866.78) * mm, "mid": v(-1732.23, 868.63) * mm, "end": v(-1730.37, 873.13) * mm});
            skPoint(sketch, "E241.visualSharp", {"position": v(-1790.7, 828.68) * mm});
            skArc(sketch, "E241.filletArc", {"start": v(-1790.7, 835.02) * mm, "mid": v(-1788.84, 830.53) * mm, "end": v(-1784.35, 828.67) * mm});
            skPoint(sketch, "E242.visualSharp", {"position": v(-1730.37, 752.48) * mm});
            skArc(sketch, "E242.filletArc", {"start": v(-1736.72, 752.48) * mm, "mid": v(-1732.23, 754.33) * mm, "end": v(-1730.37, 758.83) * mm});
            skPoint(sketch, "E243.visualSharp", {"position": v(-1790.7, 752.48) * mm});
            skArc(sketch, "E243.filletArc", {"start": v(-1784.35, 752.48) * mm, "mid": v(-1788.84, 750.62) * mm, "end": v(-1790.7, 746.12) * mm});
            skPoint(sketch, "E244.visualSharp", {"position": v(-1790.7, 714.38) * mm});
            skArc(sketch, "E244.filletArc", {"start": v(-1790.7, 720.72) * mm, "mid": v(-1788.84, 716.23) * mm, "end": v(-1784.35, 714.37) * mm});
            skPoint(sketch, "E245.visualSharp", {"position": v(-1730.37, 714.38) * mm});
            skArc(sketch, "E245.filletArc", {"start": v(-1730.37, 708.02) * mm, "mid": v(-1732.23, 712.52) * mm, "end": v(-1736.72, 714.38) * mm});
            skPoint(sketch, "E246.visualSharp", {"position": v(-1730.37, 828.68) * mm});
            skArc(sketch, "E246.filletArc", {"start": v(-1730.37, 822.32) * mm, "mid": v(-1732.23, 826.82) * mm, "end": v(-1736.72, 828.68) * mm});
            skLineSegment(sketch, "E247.bottom", {"start": v(-1717.67, 409.58) * mm, "end": v(-1730.37, 409.58) * mm});
            skLineSegment(sketch, "E247.top", {"start": v(-1717.67, 53.98) * mm, "end": v(-1730.37, 53.98) * mm});
            skLineSegment(sketch, "E247.left", {"start": v(-1717.67, 409.58) * mm, "end": v(-1717.67, 53.97) * mm});
            skLineSegment(sketch, "E247.right", {"start": v(-1730.37, 409.58) * mm, "end": v(-1730.37, 377.83) * mm});
            skLineSegment(sketch, "E248.bottom", {"start": v(-1736.72, 371.48) * mm, "end": v(-1771.65, 371.48) * mm});
            skLineSegment(sketch, "E248.top", {"start": v(-1736.72, 333.38) * mm, "end": v(-1771.65, 333.38) * mm});
            skLineSegment(sketch, "E248.right", {"start": v(-1778, 365.13) * mm, "end": v(-1778, 339.73) * mm});
            skLineSegment(sketch, "E249.bottom", {"start": v(-1771.65, 257.18) * mm, "end": v(-1736.72, 257.18) * mm});
            skLineSegment(sketch, "E249.top", {"start": v(-1771.65, 219.08) * mm, "end": v(-1736.72, 219.08) * mm});
            skLineSegment(sketch, "E249.left", {"start": v(-1778, 250.83) * mm, "end": v(-1778, 225.43) * mm});
            skLineSegment(sketch, "E250.bottom", {"start": v(-1736.72, 104.77) * mm, "end": v(-1771.65, 104.77) * mm});
            skLineSegment(sketch, "E250.top", {"start": v(-1736.72, 142.88) * mm, "end": v(-1771.65, 142.88) * mm});
            skLineSegment(sketch, "E250.right", {"start": v(-1778, 111.12) * mm, "end": v(-1778, 136.53) * mm});
            skLineSegment(sketch, "E251.trimOffspring", {"start": v(-1730.37, 327.03) * mm, "end": v(-1730.37, 263.53) * mm});
            skLineSegment(sketch, "E252.trimOffspring", {"start": v(-1730.37, 212.73) * mm, "end": v(-1730.37, 149.22) * mm});
            skLineSegment(sketch, "E253.trimOffspring", {"start": v(-1730.37, 98.42) * mm, "end": v(-1730.37, 53.97) * mm});
            skPoint(sketch, "E254.visualSharp", {"position": v(-1730.37, 371.48) * mm});
            skArc(sketch, "E254.filletArc", {"start": v(-1736.72, 371.47) * mm, "mid": v(-1732.23, 373.33) * mm, "end": v(-1730.37, 377.83) * mm});
            skPoint(sketch, "E255.visualSharp", {"position": v(-1778, 371.48) * mm});
            skArc(sketch, "E255.filletArc", {"start": v(-1771.65, 371.48) * mm, "mid": v(-1776.14, 369.62) * mm, "end": v(-1778, 365.13) * mm});
            skPoint(sketch, "E256.visualSharp", {"position": v(-1730.37, 333.38) * mm});
            skArc(sketch, "E256.filletArc", {"start": v(-1730.37, 327.03) * mm, "mid": v(-1732.23, 331.52) * mm, "end": v(-1736.72, 333.38) * mm});
            skPoint(sketch, "E257.visualSharp", {"position": v(-1778, 333.38) * mm});
            skArc(sketch, "E257.filletArc", {"start": v(-1778, 339.73) * mm, "mid": v(-1776.14, 335.23) * mm, "end": v(-1771.65, 333.37) * mm});
            skPoint(sketch, "E258.visualSharp", {"position": v(-1778, 257.18) * mm});
            skArc(sketch, "E258.filletArc", {"start": v(-1771.65, 257.18) * mm, "mid": v(-1776.14, 255.32) * mm, "end": v(-1778, 250.83) * mm});
            skPoint(sketch, "E259.visualSharp", {"position": v(-1730.37, 257.18) * mm});
            skArc(sketch, "E259.filletArc", {"start": v(-1736.72, 257.17) * mm, "mid": v(-1732.23, 259.03) * mm, "end": v(-1730.37, 263.53) * mm});
            skPoint(sketch, "E260.visualSharp", {"position": v(-1778, 219.08) * mm});
            skArc(sketch, "E260.filletArc", {"start": v(-1778, 225.43) * mm, "mid": v(-1776.14, 220.93) * mm, "end": v(-1771.65, 219.07) * mm});
            skPoint(sketch, "E261.visualSharp", {"position": v(-1730.37, 142.88) * mm});
            skArc(sketch, "E261.filletArc", {"start": v(-1736.72, 142.87) * mm, "mid": v(-1732.23, 144.73) * mm, "end": v(-1730.37, 149.22) * mm});
            skPoint(sketch, "E262.visualSharp", {"position": v(-1778, 142.87) * mm});
            skArc(sketch, "E262.filletArc", {"start": v(-1771.65, 142.88) * mm, "mid": v(-1776.14, 141.02) * mm, "end": v(-1778, 136.53) * mm});
            skPoint(sketch, "E263.visualSharp", {"position": v(-1778, 104.77) * mm});
            skArc(sketch, "E263.filletArc", {"start": v(-1778, 111.12) * mm, "mid": v(-1776.14, 106.63) * mm, "end": v(-1771.65, 104.77) * mm});
            skPoint(sketch, "E264.visualSharp", {"position": v(-1730.37, 104.77) * mm});
            skArc(sketch, "E264.filletArc", {"start": v(-1730.37, 98.42) * mm, "mid": v(-1732.23, 102.92) * mm, "end": v(-1736.72, 104.78) * mm});
            skPoint(sketch, "E265.visualSharp", {"position": v(-1730.37, 219.08) * mm});
            skArc(sketch, "E265.filletArc", {"start": v(-1730.37, 212.73) * mm, "mid": v(-1732.23, 217.22) * mm, "end": v(-1736.72, 219.08) * mm});
            skSolve(sketch);
        }
        {
            var Q0;
            Q0 = qSketchRegion(id + "F53", true);
            extrude(context, id + "F54", {"entities" : qUnion([Q0]), "depth" : 1187.45 * mm, "offsetDistance" : 25.4 * mm});
        }
        {
            var Q0;
            Q0=makeQuery(id+"F54.opExtrude","CAP_FACE",FACE,{"disambiguationData":[OSD([sQuery(id+"F53.wireOp",EDGE,"E228.bottom"),sQuery(id+"F53.wireOp",EDGE,"E228.top"),sQuery(id+"F53.wireOp",EDGE,"E228.left"),sQuery(id+"F53.wireOp",EDGE,"E228.right"),sQuery(id+"F53.wireOp",EDGE,"E229.bottom"),sQuery(id+"F53.wireOp",EDGE,"E229.top"),sQuery(id+"F53.wireOp",EDGE,"E229.right"),sQuery(id+"F53.wireOp",EDGE,"E230.bottom"),sQuery(id+"F53.wireOp",EDGE,"E230.top"),sQuery(id+"F53.wireOp",EDGE,"E230.left"),sQuery(id+"F53.wireOp",EDGE,"E231.bottom"),sQuery(id+"F53.wireOp",EDGE,"E231.top"),sQuery(id+"F53.wireOp",EDGE,"E231.right"),sQuery(id+"F53.wireOp",EDGE,"E232.trimOffspring"),sQuery(id+"F53.wireOp",EDGE,"E233.trimOffspring"),sQuery(id+"F53.wireOp",EDGE,"E234.trimOffspring"),sQuery(id+"F53.wireOp",EDGE,"E235.filletArc"),sQuery(id+"F53.wireOp",EDGE,"E236.filletArc"),sQuery(id+"F53.wireOp",EDGE,"E237.filletArc"),sQuery(id+"F53.wireOp",EDGE,"E238.filletArc"),sQuery(id+"F53.wireOp",EDGE,"E239.filletArc"),sQuery(id+"F53.wireOp",EDGE,"E240.filletArc"),sQuery(id+"F53.wireOp",EDGE,"E241.filletArc"),sQuery(id+"F53.wireOp",EDGE,"E242.filletArc"),sQuery(id+"F53.wireOp",EDGE,"E243.filletArc"),sQuery(id+"F53.wireOp",EDGE,"E244.filletArc"),sQuery(id+"F53.wireOp",EDGE,"E245.filletArc"),sQuery(id+"F53.wireOp",EDGE,"E246.filletArc")])],"isStart":false});
            var sketch = newSketch(context, id + "F55", { "sketchPlane" : qUnion([Q0])});
            skLineSegment(sketch, "E266.bottom", {"start": v(-1803.4, 1019.18) * mm, "end": v(-1714.5, 1019.18) * mm});
            skLineSegment(sketch, "E266.top", {"start": v(-1803.4, 53.97) * mm, "end": v(-1714.5, 53.97) * mm});
            skLineSegment(sketch, "E266.left", {"start": v(-1803.4, 1019.18) * mm, "end": v(-1803.4, 53.97) * mm});
            skLineSegment(sketch, "E266.right", {"start": v(-1714.5, 1019.18) * mm, "end": v(-1714.5, 53.97) * mm});
            skSolve(sketch);
        }
        {
            var Q0;
            Q0 = qSketchRegion(id + "F55", true);
            extrude(context, id + "F56", {"entities" : qUnion([Q0]), "depth" : 31.75 * mm, "offsetDistance" : 25.4 * mm});
        }
        {
            var Q0;
            Q0=makeQuery(id+"F56.opExtrude","SWEPT_FACE",FACE,{"disambiguationData":[OSD([sQuery(id+"F55.wireOp",EDGE,"E266.left")])]});
            var sketch = newSketch(context, id + "F57", { "sketchPlane" : qUnion([Q0])});
            skLineSegment(sketch, "E267.bottom", {"start": v(11461.5, 974.73) * mm, "end": v(11499.6, 974.73) * mm});
            skLineSegment(sketch, "E267.top", {"start": v(11461.5, 720.73) * mm, "end": v(11499.6, 720.73) * mm});
            skLineSegment(sketch, "E267.left", {"start": v(11455.14, 968.38) * mm, "end": v(11455.14, 727.07) * mm});
            skLineSegment(sketch, "E267.right", {"start": v(11505.94, 968.38) * mm, "end": v(11505.94, 727.07) * mm});
            skLineSegment(sketch, "E268.bottom", {"start": v(11461.5, 365.13) * mm, "end": v(11499.6, 365.13) * mm});
            skLineSegment(sketch, "E268.top", {"start": v(11461.5, 136.53) * mm, "end": v(11499.6, 136.53) * mm});
            skLineSegment(sketch, "E268.left", {"start": v(11455.14, 358.77) * mm, "end": v(11455.14, 142.87) * mm});
            skLineSegment(sketch, "E268.right", {"start": v(11505.94, 358.78) * mm, "end": v(11505.94, 142.88) * mm});
            skPoint(sketch, "E269.visualSharp", {"position": v(11455.14, 365.13) * mm});
            skArc(sketch, "E269.filletArc", {"start": v(11461.5, 365.13) * mm, "mid": v(11457, 363.27) * mm, "end": v(11455.14, 358.77) * mm});
            skPoint(sketch, "E270.visualSharp", {"position": v(11505.94, 136.53) * mm});
            skArc(sketch, "E270.filletArc", {"start": v(11499.6, 136.53) * mm, "mid": v(11504.08, 138.38) * mm, "end": v(11505.94, 142.88) * mm});
            skPoint(sketch, "E271.visualSharp", {"position": v(11505.94, 365.13) * mm});
            skArc(sketch, "E271.filletArc", {"start": v(11505.94, 358.78) * mm, "mid": v(11504.08, 363.27) * mm, "end": v(11499.6, 365.13) * mm});
            skPoint(sketch, "E272.visualSharp", {"position": v(11455.14, 974.73) * mm});
            skArc(sketch, "E272.filletArc", {"start": v(11461.5, 974.73) * mm, "mid": v(11457, 972.87) * mm, "end": v(11455.14, 968.38) * mm});
            skPoint(sketch, "E273.visualSharp", {"position": v(11505.94, 974.73) * mm});
            skArc(sketch, "E273.filletArc", {"start": v(11505.94, 968.38) * mm, "mid": v(11504.08, 972.87) * mm, "end": v(11499.6, 974.73) * mm});
            skPoint(sketch, "E274.visualSharp", {"position": v(11505.94, 720.73) * mm});
            skArc(sketch, "E274.filletArc", {"start": v(11499.6, 720.73) * mm, "mid": v(11504.08, 722.58) * mm, "end": v(11505.94, 727.07) * mm});
            skPoint(sketch, "E275.visualSharp", {"position": v(11455.14, 720.73) * mm});
            skArc(sketch, "E275.filletArc", {"start": v(11455.14, 727.07) * mm, "mid": v(11457, 722.58) * mm, "end": v(11461.5, 720.73) * mm});
            skPoint(sketch, "E276.visualSharp", {"position": v(11455.14, 136.53) * mm});
            skArc(sketch, "E276.filletArc", {"start": v(11455.14, 142.87) * mm, "mid": v(11457, 138.38) * mm, "end": v(11461.5, 136.53) * mm});
            skSolve(sketch);
        }
        {
            var Q0;
            Q0 = qSketchRegion(id + "F57", true);
            extrude(context, id + "F58", {"entities" : qUnion([Q0]), "depth" : 3.17 * mm, "offsetDistance" : 25.4 * mm});
        }
        {
            var Q0;
            Q0=makeQuery(id+"F52.opExtrude","SWEPT_FACE",FACE,{"disambiguationData":[OSD([sQuery(id+"F51.wireOp",EDGE,"E227.bottom")])]});
            var sketch = newSketch(context, id + "F59", { "sketchPlane" : qUnion([Q0])});
            skLineSegment(sketch, "E277.bottom", {"start": v(10223.24, -1714.5) * mm, "end": v(10255, -1714.5) * mm});
            skLineSegment(sketch, "E277.top", {"start": v(10223.24, -1803.4) * mm, "end": v(10255, -1803.4) * mm});
            skLineSegment(sketch, "E277.left", {"start": v(10223.24, -1714.5) * mm, "end": v(10223.24, -1803.4) * mm});
            skLineSegment(sketch, "E277.right", {"start": v(10255, -1714.5) * mm, "end": v(10255, -1803.4) * mm});
            skLineSegment(sketch, "E278.bottom", {"start": v(11442.44, -1714.5) * mm, "end": v(11474.2, -1714.5) * mm});
            skLineSegment(sketch, "E278.top", {"start": v(11442.44, -1803.4) * mm, "end": v(11474.2, -1803.4) * mm});
            skLineSegment(sketch, "E278.left", {"start": v(11442.44, -1714.5) * mm, "end": v(11442.44, -1803.4) * mm});
            skLineSegment(sketch, "E278.right", {"start": v(11474.2, -1714.5) * mm, "end": v(11474.2, -1803.4) * mm});
            skSolve(sketch);
        }
        {
            var Q0;
            Q0 = qSketchRegion(id + "F59", true);
            extrude(context, id + "F60", {"entities" : qUnion([Q0]), "depth" : 9.52 * mm, "offsetDistance" : 25.4 * mm});
        }
        {
            var Q0;
            Q0=makeQuery(id+"F60.opExtrude","CAP_EDGE",EDGE,{"disambiguationData":[OSD([sQuery(id+"F59.wireOp",EDGE,"E277.right")])],"isStart":false});
            var Q1;
            Q1=makeQuery(id+"F60.opExtrude","CAP_EDGE",EDGE,{"disambiguationData":[OSD([sQuery(id+"F59.wireOp",EDGE,"E277.top")])],"isStart":false});
            var Q2;
            Q2=makeQuery(id+"F60.opExtrude","CAP_EDGE",EDGE,{"disambiguationData":[OSD([sQuery(id+"F59.wireOp",EDGE,"E277.left")])],"isStart":false});
            var Q3;
            Q3=makeQuery(id+"F60.opExtrude","CAP_EDGE",EDGE,{"disambiguationData":[OSD([sQuery(id+"F59.wireOp",EDGE,"E277.bottom")])],"isStart":false});
            var Q4;
            Q4=makeQuery(id+"F60.opExtrude","CAP_EDGE",EDGE,{"disambiguationData":[OSD([sQuery(id+"F59.wireOp",EDGE,"E278.left")])],"isStart":false});
            var Q5;
            Q5=makeQuery(id+"F60.opExtrude","CAP_EDGE",EDGE,{"disambiguationData":[OSD([sQuery(id+"F59.wireOp",EDGE,"E278.top")])],"isStart":false});
            var Q6;
            Q6=makeQuery(id+"F60.opExtrude","CAP_EDGE",EDGE,{"disambiguationData":[OSD([sQuery(id+"F59.wireOp",EDGE,"E278.right")])],"isStart":false});
            var Q7;
            Q7=makeQuery(id+"F60.opExtrude","CAP_EDGE",EDGE,{"disambiguationData":[OSD([sQuery(id+"F59.wireOp",EDGE,"E278.bottom")])],"isStart":false});
            chamfer(context, id + "F61", {"entities" : qUnion([Q0, Q1, Q2, Q3, Q4, Q5, Q6, Q7]), "width" : 3.8 * mm, "tangentPropagation" : true});
        }
        {
            var Q0;
            Q0=makeQuery(id+"F7.opExtrude","SWEPT_FACE",FACE,{"disambiguationData":[OSD([sQuery(id+"F6.wireOp",EDGE,"E18.right")])]});
            var Q1;
            Q1=makeQuery(id+"F7.opExtrude","SWEPT_FACE",FACE,{"disambiguationData":[OSD([sQuery(id+"F6.wireOp",EDGE,"E19.left")])]});
            cPlane(context, id + "F62", {"entities" : qUnion([Q0, Q1]), "cplaneType" : CPlaneType.MID_PLANE, "offset" : 25.4 * mm, "width" : 152.4 * mm, "height" : 152.4 * mm});
        }
        {
            var Q0;
            Q0=makeQuery(id+"F13.opExtrude","SWEPT_BODY",BODY,{"disambiguationData":[OSD([sQuery(id+"F12.wireOp",EDGE,"E36.bottom"),sQuery(id+"F12.wireOp",EDGE,"E36.top"),sQuery(id+"F12.wireOp",EDGE,"E36.left"),sQuery(id+"F12.wireOp",EDGE,"E36.right")])]});
            var Q1;
            Q1=makeQuery(id+"F17.opExtrude","SWEPT_BODY",BODY,{"disambiguationData":[OSD([sQuery(id+"F16.wireOp",EDGE,"E46.bottom"),sQuery(id+"F16.wireOp",EDGE,"E46.top"),sQuery(id+"F16.wireOp",EDGE,"E46.left"),sQuery(id+"F16.wireOp",EDGE,"E46.right")])]});
            var Q2;
            Q2=makeQuery(id+"F28.opExtrude","SWEPT_BODY",BODY,{"disambiguationData":[OSD([sQuery(id+"F27.wireOp",EDGE,"E191"),sQuery(id+"F27.wireOp",EDGE,"E192"),sQuery(id+"F27.wireOp",EDGE,"E193"),sQuery(id+"F27.wireOp",EDGE,"E194"),sQuery(id+"F27.wireOp",EDGE,"E195"),sQuery(id+"F27.wireOp",EDGE,"E196"),sQuery(id+"F27.wireOp",EDGE,"E197"),sQuery(id+"F27.wireOp",EDGE,"E198"),sQuery(id+"F27.wireOp",EDGE,"E199"),sQuery(id+"F27.wireOp",EDGE,"E200"),sQuery(id+"F27.wireOp",EDGE,"E201"),sQuery(id+"F27.wireOp",EDGE,"E202"),sQuery(id+"F27.wireOp",EDGE,"E203"),sQuery(id+"F27.wireOp",EDGE,"E204"),sQuery(id+"F27.wireOp",EDGE,"E205"),sQuery(id+"F27.wireOp",EDGE,"E206")])]});
            var Q3;
            Q3=makeQuery(id+"F28.opExtrude","SWEPT_BODY",BODY,{"disambiguationData":[OSD([sQuery(id+"F27.wireOp",EDGE,"E175"),sQuery(id+"F27.wireOp",EDGE,"E176"),sQuery(id+"F27.wireOp",EDGE,"E177"),sQuery(id+"F27.wireOp",EDGE,"E178"),sQuery(id+"F27.wireOp",EDGE,"E179"),sQuery(id+"F27.wireOp",EDGE,"E180"),sQuery(id+"F27.wireOp",EDGE,"E181"),sQuery(id+"F27.wireOp",EDGE,"E182"),sQuery(id+"F27.wireOp",EDGE,"E183"),sQuery(id+"F27.wireOp",EDGE,"E184"),sQuery(id+"F27.wireOp",EDGE,"E185"),sQuery(id+"F27.wireOp",EDGE,"E186"),sQuery(id+"F27.wireOp",EDGE,"E187"),sQuery(id+"F27.wireOp",EDGE,"E188"),sQuery(id+"F27.wireOp",EDGE,"E189"),sQuery(id+"F27.wireOp",EDGE,"E190")])]});
            var Q4;
            Q4=makeQuery(id+"F13.opExtrude","SWEPT_BODY",BODY,{"disambiguationData":[OSD([sQuery(id+"F12.wireOp",EDGE,"E35.bottom"),sQuery(id+"F12.wireOp",EDGE,"E35.top"),sQuery(id+"F12.wireOp",EDGE,"E35.left"),sQuery(id+"F12.wireOp",EDGE,"E35.right")])]});
            var Q5;
            Q5=makeQuery(id+"F17.opExtrude","SWEPT_BODY",BODY,{"disambiguationData":[OSD([sQuery(id+"F16.wireOp",EDGE,"E45.bottom"),sQuery(id+"F16.wireOp",EDGE,"E45.top"),sQuery(id+"F16.wireOp",EDGE,"E45.left"),sQuery(id+"F16.wireOp",EDGE,"E45.right")])]});
            var Q6;
            Q6=makeQuery(id+"F5.opExtrude","SWEPT_BODY",BODY,{"disambiguationData":[OSD([sQuery(id+"F4.wireOp",EDGE,"E10.bottom"),sQuery(id+"F4.wireOp",EDGE,"E10.top"),sQuery(id+"F4.wireOp",EDGE,"E10.left"),sQuery(id+"F4.wireOp",EDGE,"E10.right")])]});
            var Q7;
            Q7=makeQuery(id+"F13.opExtrude","SWEPT_BODY",BODY,{"disambiguationData":[OSD([sQuery(id+"F12.wireOp",EDGE,"E34.bottom"),sQuery(id+"F12.wireOp",EDGE,"E34.top"),sQuery(id+"F12.wireOp",EDGE,"E34.left"),sQuery(id+"F12.wireOp",EDGE,"E34.right")])]});
            var Q8;
            Q8=makeQuery(id+"F17.opExtrude","SWEPT_BODY",BODY,{"disambiguationData":[OSD([sQuery(id+"F16.wireOp",EDGE,"E44.bottom"),sQuery(id+"F16.wireOp",EDGE,"E44.top"),sQuery(id+"F16.wireOp",EDGE,"E44.left"),sQuery(id+"F16.wireOp",EDGE,"E44.right")])]});
            var Q9;
            Q9=makeQuery(id+"F26.opExtrude","SWEPT_BODY",BODY,{"disambiguationData":[OSD([sQuery(id+"F25.wireOp",EDGE,"E159"),sQuery(id+"F25.wireOp",EDGE,"E160"),sQuery(id+"F25.wireOp",EDGE,"E161"),sQuery(id+"F25.wireOp",EDGE,"E162"),sQuery(id+"F25.wireOp",EDGE,"E163"),sQuery(id+"F25.wireOp",EDGE,"E164"),sQuery(id+"F25.wireOp",EDGE,"E165"),sQuery(id+"F25.wireOp",EDGE,"E166"),sQuery(id+"F25.wireOp",EDGE,"E167"),sQuery(id+"F25.wireOp",EDGE,"E168"),sQuery(id+"F25.wireOp",EDGE,"E169"),sQuery(id+"F25.wireOp",EDGE,"E170"),sQuery(id+"F25.wireOp",EDGE,"E171"),sQuery(id+"F25.wireOp",EDGE,"E172"),sQuery(id+"F25.wireOp",EDGE,"E173"),sQuery(id+"F25.wireOp",EDGE,"E174")])]});
            var Q10;
            Q10=makeQuery(id+"F26.opExtrude","SWEPT_BODY",BODY,{"disambiguationData":[OSD([sQuery(id+"F25.wireOp",EDGE,"E143"),sQuery(id+"F25.wireOp",EDGE,"E144"),sQuery(id+"F25.wireOp",EDGE,"E145"),sQuery(id+"F25.wireOp",EDGE,"E146"),sQuery(id+"F25.wireOp",EDGE,"E147"),sQuery(id+"F25.wireOp",EDGE,"E148"),sQuery(id+"F25.wireOp",EDGE,"E149"),sQuery(id+"F25.wireOp",EDGE,"E150"),sQuery(id+"F25.wireOp",EDGE,"E151"),sQuery(id+"F25.wireOp",EDGE,"E152"),sQuery(id+"F25.wireOp",EDGE,"E153"),sQuery(id+"F25.wireOp",EDGE,"E154"),sQuery(id+"F25.wireOp",EDGE,"E155"),sQuery(id+"F25.wireOp",EDGE,"E156"),sQuery(id+"F25.wireOp",EDGE,"E157"),sQuery(id+"F25.wireOp",EDGE,"E158")])]});
            var Q11;
            Q11=makeQuery(id+"F10.opExtrude","SWEPT_BODY",BODY,{"disambiguationData":[OSD([sQuery(id+"F9.wireOp",EDGE,"E24.bottom"),sQuery(id+"F9.wireOp",EDGE,"E24.top"),sQuery(id+"F9.wireOp",EDGE,"E24.left"),sQuery(id+"F9.wireOp",EDGE,"E24.right")])]});
            var Q12;
            Q12=makeQuery(id+"F13.opExtrude","SWEPT_BODY",BODY,{"disambiguationData":[OSD([sQuery(id+"F12.wireOp",EDGE,"E32.bottom"),sQuery(id+"F12.wireOp",EDGE,"E32.top"),sQuery(id+"F12.wireOp",EDGE,"E32.left"),sQuery(id+"F12.wireOp",EDGE,"E32.right")])]});
            var Q13;
            Q13=makeQuery(id+"F17.opExtrude","SWEPT_BODY",BODY,{"disambiguationData":[OSD([sQuery(id+"F16.wireOp",EDGE,"E42.bottom"),sQuery(id+"F16.wireOp",EDGE,"E42.top"),sQuery(id+"F16.wireOp",EDGE,"E42.left"),sQuery(id+"F16.wireOp",EDGE,"E42.right")])]});
            var Q14;
            Q14=makeQuery(id+"F24.opExtrude","SWEPT_BODY",BODY,{"disambiguationData":[OSD([sQuery(id+"F23.wireOp",EDGE,"E127"),sQuery(id+"F23.wireOp",EDGE,"E128"),sQuery(id+"F23.wireOp",EDGE,"E129"),sQuery(id+"F23.wireOp",EDGE,"E130"),sQuery(id+"F23.wireOp",EDGE,"E131"),sQuery(id+"F23.wireOp",EDGE,"E132"),sQuery(id+"F23.wireOp",EDGE,"E133"),sQuery(id+"F23.wireOp",EDGE,"E134"),sQuery(id+"F23.wireOp",EDGE,"E135"),sQuery(id+"F23.wireOp",EDGE,"E136"),sQuery(id+"F23.wireOp",EDGE,"E137"),sQuery(id+"F23.wireOp",EDGE,"E138"),sQuery(id+"F23.wireOp",EDGE,"E139"),sQuery(id+"F23.wireOp",EDGE,"E140"),sQuery(id+"F23.wireOp",EDGE,"E141"),sQuery(id+"F23.wireOp",EDGE,"E142")])]});
            var Q15;
            Q15=makeQuery(id+"F24.opExtrude","SWEPT_BODY",BODY,{"disambiguationData":[OSD([sQuery(id+"F23.wireOp",EDGE,"E111"),sQuery(id+"F23.wireOp",EDGE,"E112"),sQuery(id+"F23.wireOp",EDGE,"E113"),sQuery(id+"F23.wireOp",EDGE,"E114"),sQuery(id+"F23.wireOp",EDGE,"E115"),sQuery(id+"F23.wireOp",EDGE,"E116"),sQuery(id+"F23.wireOp",EDGE,"E117"),sQuery(id+"F23.wireOp",EDGE,"E118"),sQuery(id+"F23.wireOp",EDGE,"E119"),sQuery(id+"F23.wireOp",EDGE,"E120"),sQuery(id+"F23.wireOp",EDGE,"E121"),sQuery(id+"F23.wireOp",EDGE,"E122"),sQuery(id+"F23.wireOp",EDGE,"E123"),sQuery(id+"F23.wireOp",EDGE,"E124"),sQuery(id+"F23.wireOp",EDGE,"E125"),sQuery(id+"F23.wireOp",EDGE,"E126")])]});
            var Q16;
            Q16=makeQuery(id+"F13.opExtrude","SWEPT_BODY",BODY,{"disambiguationData":[OSD([sQuery(id+"F12.wireOp",EDGE,"E31.bottom"),sQuery(id+"F12.wireOp",EDGE,"E31.top"),sQuery(id+"F12.wireOp",EDGE,"E31.left"),sQuery(id+"F12.wireOp",EDGE,"E31.right")])]});
            var Q17;
            Q17=makeQuery(id+"F17.opExtrude","SWEPT_BODY",BODY,{"disambiguationData":[OSD([sQuery(id+"F16.wireOp",EDGE,"E41.bottom"),sQuery(id+"F16.wireOp",EDGE,"E41.top"),sQuery(id+"F16.wireOp",EDGE,"E41.left"),sQuery(id+"F16.wireOp",EDGE,"E41.right")])]});
            var Q18;
            Q18=makeQuery(id+"F5.opExtrude","SWEPT_BODY",BODY,{"disambiguationData":[OSD([sQuery(id+"F4.wireOp",EDGE,"E8.bottom"),sQuery(id+"F4.wireOp",EDGE,"E8.top"),sQuery(id+"F4.wireOp",EDGE,"E8.left"),sQuery(id+"F4.wireOp",EDGE,"E8.right")])]});
            var Q19;
            Q19=makeQuery(id+"F13.opExtrude","SWEPT_BODY",BODY,{"disambiguationData":[OSD([sQuery(id+"F12.wireOp",EDGE,"E30.bottom"),sQuery(id+"F12.wireOp",EDGE,"E30.top"),sQuery(id+"F12.wireOp",EDGE,"E30.left"),sQuery(id+"F12.wireOp",EDGE,"E30.right")])]});
            var Q20;
            Q20=makeQuery(id+"F17.opExtrude","SWEPT_BODY",BODY,{"disambiguationData":[OSD([sQuery(id+"F16.wireOp",EDGE,"E40.bottom"),sQuery(id+"F16.wireOp",EDGE,"E40.top"),sQuery(id+"F16.wireOp",EDGE,"E40.left"),sQuery(id+"F16.wireOp",EDGE,"E40.right")])]});
            var Q21;
            Q21=makeQuery(id+"F22.opExtrude","SWEPT_BODY",BODY,{"disambiguationData":[OSD([sQuery(id+"F21.wireOp",EDGE,"E79"),sQuery(id+"F21.wireOp",EDGE,"E80"),sQuery(id+"F21.wireOp",EDGE,"E81"),sQuery(id+"F21.wireOp",EDGE,"E82"),sQuery(id+"F21.wireOp",EDGE,"E83"),sQuery(id+"F21.wireOp",EDGE,"E84"),sQuery(id+"F21.wireOp",EDGE,"E85"),sQuery(id+"F21.wireOp",EDGE,"E86"),sQuery(id+"F21.wireOp",EDGE,"E87"),sQuery(id+"F21.wireOp",EDGE,"E88"),sQuery(id+"F21.wireOp",EDGE,"E89"),sQuery(id+"F21.wireOp",EDGE,"E90"),sQuery(id+"F21.wireOp",EDGE,"E91"),sQuery(id+"F21.wireOp",EDGE,"E92"),sQuery(id+"F21.wireOp",EDGE,"E93"),sQuery(id+"F21.wireOp",EDGE,"E94")])]});
            var Q22;
            Q22=makeQuery(id+"F22.opExtrude","SWEPT_BODY",BODY,{"disambiguationData":[OSD([sQuery(id+"F21.wireOp",EDGE,"E95"),sQuery(id+"F21.wireOp",EDGE,"E96"),sQuery(id+"F21.wireOp",EDGE,"E97"),sQuery(id+"F21.wireOp",EDGE,"E98"),sQuery(id+"F21.wireOp",EDGE,"E99"),sQuery(id+"F21.wireOp",EDGE,"E100"),sQuery(id+"F21.wireOp",EDGE,"E101"),sQuery(id+"F21.wireOp",EDGE,"E102"),sQuery(id+"F21.wireOp",EDGE,"E103"),sQuery(id+"F21.wireOp",EDGE,"E104"),sQuery(id+"F21.wireOp",EDGE,"E105"),sQuery(id+"F21.wireOp",EDGE,"E106"),sQuery(id+"F21.wireOp",EDGE,"E107"),sQuery(id+"F21.wireOp",EDGE,"E108"),sQuery(id+"F21.wireOp",EDGE,"E109"),sQuery(id+"F21.wireOp",EDGE,"E110")])]});
            var Q23;
            Q23=makeQuery(id+"F5.opExtrude","SWEPT_BODY",BODY,{"disambiguationData":[OSD([sQuery(id+"F4.wireOp",EDGE,"E6.bottom"),sQuery(id+"F4.wireOp",EDGE,"E6.top"),sQuery(id+"F4.wireOp",EDGE,"E6.left"),sQuery(id+"F4.wireOp",EDGE,"E6.right")])]});
            var Q24;
            Q24=makeQuery(id+"F10.opExtrude","SWEPT_BODY",BODY,{"disambiguationData":[OSD([sQuery(id+"F9.wireOp",EDGE,"E21.bottom"),sQuery(id+"F9.wireOp",EDGE,"E21.top"),sQuery(id+"F9.wireOp",EDGE,"E21.left"),sQuery(id+"F9.wireOp",EDGE,"E21.right")])]});
            var Q25;
            Q25=makeQuery(id+"F10.opExtrude","SWEPT_BODY",BODY,{"disambiguationData":[OSD([sQuery(id+"F9.wireOp",EDGE,"E22.bottom"),sQuery(id+"F9.wireOp",EDGE,"E22.top"),sQuery(id+"F9.wireOp",EDGE,"E22.left"),sQuery(id+"F9.wireOp",EDGE,"E22.right")])]});
            var Q26;
            Q26=makeQuery(id+"F10.opExtrude","SWEPT_BODY",BODY,{"disambiguationData":[OSD([sQuery(id+"F9.wireOp",EDGE,"E23.bottom"),sQuery(id+"F9.wireOp",EDGE,"E23.top"),sQuery(id+"F9.wireOp",EDGE,"E23.left"),sQuery(id+"F9.wireOp",EDGE,"E23.right")])]});
            var Q27;
            Q27=makeQuery(id+"F13.opExtrude","SWEPT_BODY",BODY,{"disambiguationData":[OSD([sQuery(id+"F12.wireOp",EDGE,"E29.bottom"),sQuery(id+"F12.wireOp",EDGE,"E29.top"),sQuery(id+"F12.wireOp",EDGE,"E29.left"),sQuery(id+"F12.wireOp",EDGE,"E29.right")])]});
            var Q28;
            Q28=makeQuery(id+"F17.opExtrude","SWEPT_BODY",BODY,{"disambiguationData":[OSD([sQuery(id+"F16.wireOp",EDGE,"E39.bottom"),sQuery(id+"F16.wireOp",EDGE,"E39.top"),sQuery(id+"F16.wireOp",EDGE,"E39.left"),sQuery(id+"F16.wireOp",EDGE,"E39.right")])]});
            var Q29;
            Q29=makeQuery(id+"F5.opExtrude","SWEPT_BODY",BODY,{"disambiguationData":[OSD([sQuery(id+"F4.wireOp",EDGE,"E9.bottom"),sQuery(id+"F4.wireOp",EDGE,"E9.top"),sQuery(id+"F4.wireOp",EDGE,"E9.left"),sQuery(id+"F4.wireOp",EDGE,"E9.right")])]});
            var Q30;
            Q30=makeQuery(id+"F13.opExtrude","SWEPT_BODY",BODY,{"disambiguationData":[OSD([sQuery(id+"F12.wireOp",EDGE,"E33.bottom"),sQuery(id+"F12.wireOp",EDGE,"E33.top"),sQuery(id+"F12.wireOp",EDGE,"E33.left"),sQuery(id+"F12.wireOp",EDGE,"E33.right")])]});
            var Q31;
            Q31=makeQuery(id+"F17.opExtrude","SWEPT_BODY",BODY,{"disambiguationData":[OSD([sQuery(id+"F16.wireOp",EDGE,"E43.bottom"),sQuery(id+"F16.wireOp",EDGE,"E43.top"),sQuery(id+"F16.wireOp",EDGE,"E43.left"),sQuery(id+"F16.wireOp",EDGE,"E43.right")])]});
            var Q32;
            Q32=qCreatedBy(id+"F62.planeOp",FACE);
            mirror(context, id + "F63", {"entities" : qUnion([Q0, Q1, Q2, Q3, Q4, Q5, Q6, Q7, Q8, Q9, Q10, Q11, Q12, Q13, Q14, Q15, Q16, Q17, Q18, Q19, Q20, Q21, Q22, Q23, Q24, Q25, Q26, Q27, Q28, Q29, Q30, Q31]), "mirrorPlane" : qUnion([Q32])});
        }
        {
            var Q0;
            Q0=makeQuery(id+"F63.opPattern","COPY",FACE,{"derivedFrom":makeQuery(id+"F7.opExtrude","SWEPT_FACE",FACE,{"disambiguationData":[OSD([sQuery(id+"F6.wireOp",EDGE,"E14.left")])]}),"instanceName":"1"});
            var Q1;
            Q1=makeQuery(id+"F63.opPattern","COPY",FACE,{"derivedFrom":makeQuery(id+"F7.opExtrude","SWEPT_FACE",FACE,{"disambiguationData":[OSD([sQuery(id+"F6.wireOp",EDGE,"E14.right")])]}),"instanceName":"1"});
            cPlane(context, id + "F64", {"entities" : qUnion([Q0, Q1]), "cplaneType" : CPlaneType.MID_PLANE, "offset" : 25.4 * mm, "width" : 152.4 * mm, "height" : 152.4 * mm});
        }
        {
            var Q0;
            Q0=makeQuery(id+"F63.opPattern","COPY",BODY,{"derivedFrom":makeQuery(id+"F13.opExtrude","SWEPT_BODY",BODY,{"disambiguationData":[OSD([sQuery(id+"F12.wireOp",EDGE,"E29.bottom"),sQuery(id+"F12.wireOp",EDGE,"E29.top"),sQuery(id+"F12.wireOp",EDGE,"E29.left"),sQuery(id+"F12.wireOp",EDGE,"E29.right")])]}),"instanceName":"1"});
            var Q1;
            Q1=makeQuery(id+"F63.opPattern","COPY",BODY,{"derivedFrom":makeQuery(id+"F22.opExtrude","SWEPT_BODY",BODY,{"disambiguationData":[OSD([sQuery(id+"F21.wireOp",EDGE,"E95"),sQuery(id+"F21.wireOp",EDGE,"E96"),sQuery(id+"F21.wireOp",EDGE,"E97"),sQuery(id+"F21.wireOp",EDGE,"E98"),sQuery(id+"F21.wireOp",EDGE,"E99"),sQuery(id+"F21.wireOp",EDGE,"E100"),sQuery(id+"F21.wireOp",EDGE,"E101"),sQuery(id+"F21.wireOp",EDGE,"E102"),sQuery(id+"F21.wireOp",EDGE,"E103"),sQuery(id+"F21.wireOp",EDGE,"E104"),sQuery(id+"F21.wireOp",EDGE,"E105"),sQuery(id+"F21.wireOp",EDGE,"E106"),sQuery(id+"F21.wireOp",EDGE,"E107"),sQuery(id+"F21.wireOp",EDGE,"E108"),sQuery(id+"F21.wireOp",EDGE,"E109"),sQuery(id+"F21.wireOp",EDGE,"E110")])]}),"instanceName":"1"});
            var Q2;
            Q2=makeQuery(id+"F63.opPattern","COPY",BODY,{"derivedFrom":makeQuery(id+"F22.opExtrude","SWEPT_BODY",BODY,{"disambiguationData":[OSD([sQuery(id+"F21.wireOp",EDGE,"E79"),sQuery(id+"F21.wireOp",EDGE,"E80"),sQuery(id+"F21.wireOp",EDGE,"E81"),sQuery(id+"F21.wireOp",EDGE,"E82"),sQuery(id+"F21.wireOp",EDGE,"E83"),sQuery(id+"F21.wireOp",EDGE,"E84"),sQuery(id+"F21.wireOp",EDGE,"E85"),sQuery(id+"F21.wireOp",EDGE,"E86"),sQuery(id+"F21.wireOp",EDGE,"E87"),sQuery(id+"F21.wireOp",EDGE,"E88"),sQuery(id+"F21.wireOp",EDGE,"E89"),sQuery(id+"F21.wireOp",EDGE,"E90"),sQuery(id+"F21.wireOp",EDGE,"E91"),sQuery(id+"F21.wireOp",EDGE,"E92"),sQuery(id+"F21.wireOp",EDGE,"E93"),sQuery(id+"F21.wireOp",EDGE,"E94")])]}),"instanceName":"1"});
            var Q3;
            Q3=makeQuery(id+"F63.opPattern","COPY",BODY,{"derivedFrom":makeQuery(id+"F13.opExtrude","SWEPT_BODY",BODY,{"disambiguationData":[OSD([sQuery(id+"F12.wireOp",EDGE,"E30.bottom"),sQuery(id+"F12.wireOp",EDGE,"E30.top"),sQuery(id+"F12.wireOp",EDGE,"E30.left"),sQuery(id+"F12.wireOp",EDGE,"E30.right")])]}),"instanceName":"1"});
            var Q4;
            Q4=makeQuery(id+"F63.opPattern","COPY",BODY,{"derivedFrom":makeQuery(id+"F17.opExtrude","SWEPT_BODY",BODY,{"disambiguationData":[OSD([sQuery(id+"F16.wireOp",EDGE,"E40.bottom"),sQuery(id+"F16.wireOp",EDGE,"E40.top"),sQuery(id+"F16.wireOp",EDGE,"E40.left"),sQuery(id+"F16.wireOp",EDGE,"E40.right")])]}),"instanceName":"1"});
            var Q5;
            Q5=makeQuery(id+"F63.opPattern","COPY",BODY,{"derivedFrom":makeQuery(id+"F5.opExtrude","SWEPT_BODY",BODY,{"disambiguationData":[OSD([sQuery(id+"F4.wireOp",EDGE,"E8.bottom"),sQuery(id+"F4.wireOp",EDGE,"E8.top"),sQuery(id+"F4.wireOp",EDGE,"E8.left"),sQuery(id+"F4.wireOp",EDGE,"E8.right")])]}),"instanceName":"1"});
            var Q6;
            Q6=qCreatedBy(id+"F64.planeOp",FACE);
            mirror(context, id + "F65", {"entities" : qUnion([Q0, Q1, Q2, Q3, Q4, Q5]), "mirrorPlane" : qUnion([Q6])});
        }
    });
